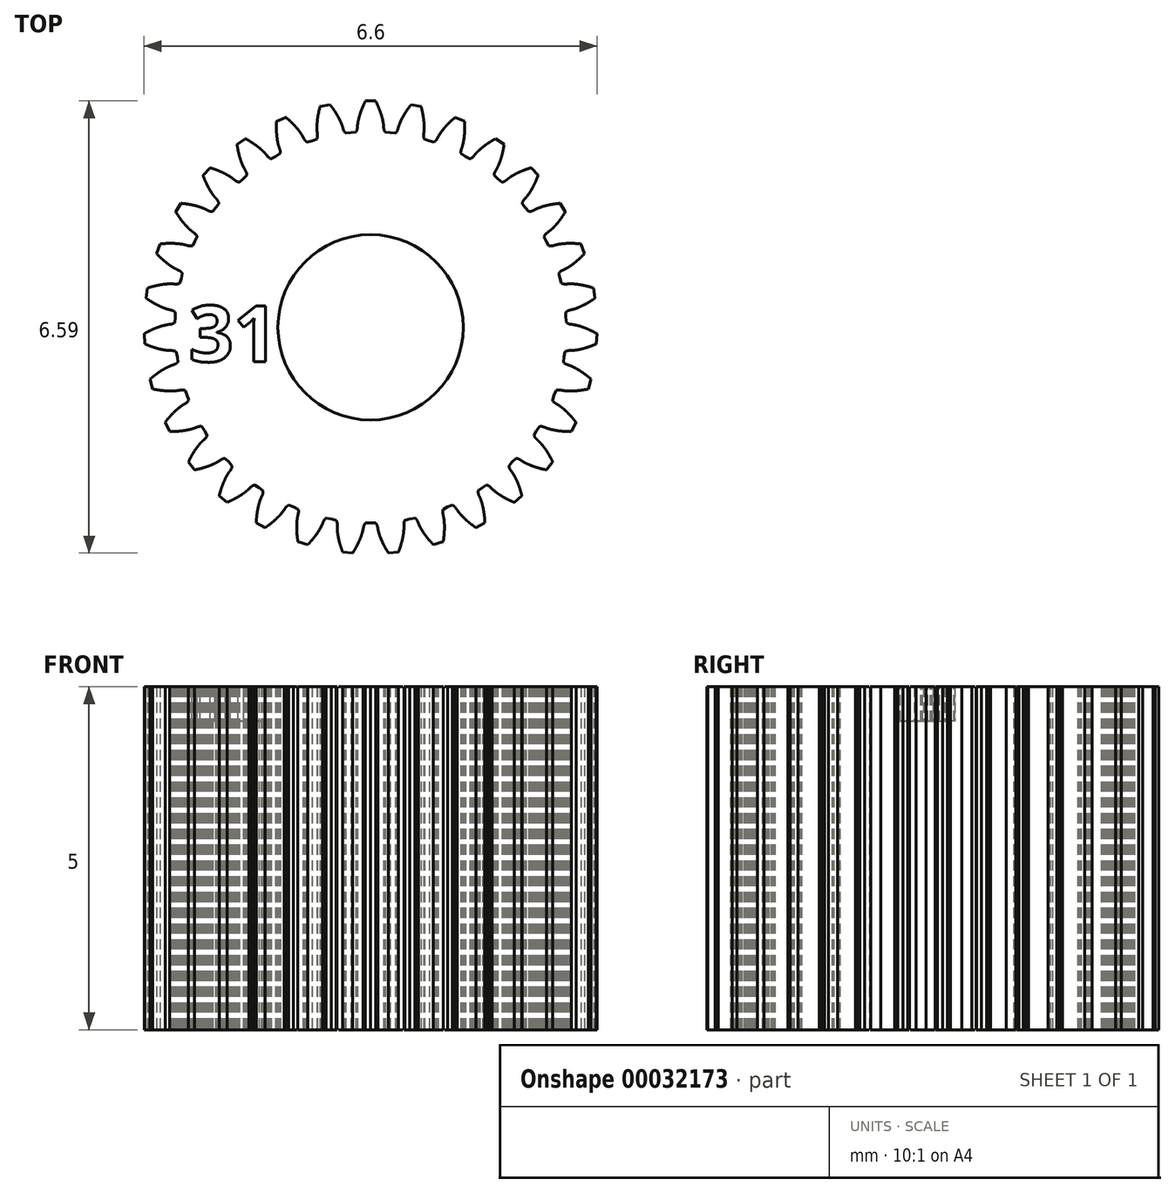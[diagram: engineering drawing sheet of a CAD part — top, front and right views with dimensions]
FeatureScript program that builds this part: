
annotation { "Feature Type Name" : "Feature", "Feature Type Description" : "" }
export const myFeature = defineFeature(function(context is Context, id is Id, definition is map)
    precondition{}
    {
        {
            var Q0;
            Q0=qCreatedBy(makeId("Top.planeOp"),FACE);
            var sketch = newSketch(context, id + "F0", { "sketchPlane" : qUnion([Q0])});
            skCircle(sketch, "E0", {"center": v(0, 0) * mm, "radius": 32.06 * mm});
            skCircle(sketch, "E1", {"center": v(0, 0) * mm, "radius": 0.2 * mm});
            skCircle(sketch, "E2", {"center": v(0, 0) * mm, "radius": 10.35 * mm});
            skCircle(sketch, "E3", {"center": v(0, 6.3) * mm, "radius": 0.2 * mm});
            skCircle(sketch, "E4", {"center": v(5.46, -3.15) * mm, "radius": 0.2 * mm});
            skCircle(sketch, "E5", {"center": v(-5.46, -3.15) * mm, "radius": 0.2 * mm});
            skLineSegment(sketch, "E6", {"start": v(0.26, 9.75) * mm, "end": v(0.26, 9.74) * mm});
            skLineSegment(sketch, "E7", {"start": v(0.26, 9.74) * mm, "end": v(0.26, 9.74) * mm});
            skLineSegment(sketch, "E8", {"start": v(0.26, 9.74) * mm, "end": v(0.26, 9.73) * mm});
            skLineSegment(sketch, "E9", {"start": v(0.26, 9.73) * mm, "end": v(0.25, 9.73) * mm});
            skLineSegment(sketch, "E10", {"start": v(0.25, 9.73) * mm, "end": v(0.25, 9.72) * mm});
            skLineSegment(sketch, "E11", {"start": v(0.25, 9.72) * mm, "end": v(0.25, 9.72) * mm});
            skLineSegment(sketch, "E12", {"start": v(0.25, 9.72) * mm, "end": v(0.25, 9.71) * mm});
            skLineSegment(sketch, "E13", {"start": v(0.25, 9.71) * mm, "end": v(0.24, 9.7) * mm});
            skLineSegment(sketch, "E14", {"start": v(0.24, 9.7) * mm, "end": v(0.24, 9.7) * mm});
            skLineSegment(sketch, "E15", {"start": v(0.24, 9.7) * mm, "end": v(0.24, 9.69) * mm});
            skLineSegment(sketch, "E16", {"start": v(0.24, 9.69) * mm, "end": v(0.23, 9.68) * mm});
            skLineSegment(sketch, "E17", {"start": v(0.23, 9.68) * mm, "end": v(0.23, 9.68) * mm});
            skLineSegment(sketch, "E18", {"start": v(0.23, 9.68) * mm, "end": v(0.23, 9.67) * mm});
            skLineSegment(sketch, "E19", {"start": v(0.23, 9.67) * mm, "end": v(0.23, 9.67) * mm});
            skLineSegment(sketch, "E20", {"start": v(0.23, 9.67) * mm, "end": v(0.22, 9.66) * mm});
            skLineSegment(sketch, "E21", {"start": v(0.22, 9.66) * mm, "end": v(0.22, 9.66) * mm});
            skLineSegment(sketch, "E22", {"start": v(0.22, 9.66) * mm, "end": v(0.22, 9.65) * mm});
            skLineSegment(sketch, "E23", {"start": v(0.22, 9.65) * mm, "end": v(0.22, 9.65) * mm});
            skLineSegment(sketch, "E24", {"start": v(0.22, 9.65) * mm, "end": v(0.22, 9.64) * mm});
            skLineSegment(sketch, "E25", {"start": v(0.22, 9.64) * mm, "end": v(0.21, 9.64) * mm});
            skLineSegment(sketch, "E26", {"start": v(0.21, 9.64) * mm, "end": v(0.21, 9.64) * mm});
            skLineSegment(sketch, "E27", {"start": v(0.21, 9.64) * mm, "end": v(0.21, 9.63) * mm});
            skLineSegment(sketch, "E28", {"start": v(0.21, 9.63) * mm, "end": v(0.2, 9.63) * mm});
            skLineSegment(sketch, "E29", {"start": v(0.2, 9.63) * mm, "end": v(0.2, 9.62) * mm});
            skLineSegment(sketch, "E30", {"start": v(0.2, 9.62) * mm, "end": v(0.2, 9.62) * mm});
            skLineSegment(sketch, "E31", {"start": v(0.2, 9.62) * mm, "end": v(0.2, 9.61) * mm});
            skLineSegment(sketch, "E32", {"start": v(0.2, 9.61) * mm, "end": v(0.2, 9.6) * mm});
            skLineSegment(sketch, "E33", {"start": v(0.2, 9.6) * mm, "end": v(0.2, 9.6) * mm});
            skLineSegment(sketch, "E34", {"start": v(0.2, 9.6) * mm, "end": v(0.2, 9.59) * mm});
            skLineSegment(sketch, "E35", {"start": v(0.2, 9.59) * mm, "end": v(0.2, 9.58) * mm});
            skLineSegment(sketch, "E36", {"start": v(0.2, 9.58) * mm, "end": v(0.19, 9.58) * mm});
            skLineSegment(sketch, "E37", {"start": v(0.19, 9.58) * mm, "end": v(0.19, 9.57) * mm});
            skLineSegment(sketch, "E38", {"start": v(0.19, 9.57) * mm, "end": v(0.18, 9.57) * mm});
            skLineSegment(sketch, "E39", {"start": v(0.18, 9.57) * mm, "end": v(0.18, 9.56) * mm});
            skLineSegment(sketch, "E40", {"start": v(0.18, 9.56) * mm, "end": v(0.18, 9.56) * mm});
            skLineSegment(sketch, "E41", {"start": v(0.18, 9.56) * mm, "end": v(0.18, 9.55) * mm});
            skLineSegment(sketch, "E42", {"start": v(0.18, 9.55) * mm, "end": v(0.18, 9.55) * mm});
            skLineSegment(sketch, "E43", {"start": v(0.18, 9.55) * mm, "end": v(0.17, 9.54) * mm});
            skLineSegment(sketch, "E44", {"start": v(0.17, 9.54) * mm, "end": v(0.17, 9.54) * mm});
            skLineSegment(sketch, "E45", {"start": v(0.17, 9.54) * mm, "end": v(0.17, 9.53) * mm});
            skLineSegment(sketch, "E46", {"start": v(0.17, 9.53) * mm, "end": v(0.17, 9.53) * mm});
            skLineSegment(sketch, "E47", {"start": v(0.17, 9.53) * mm, "end": v(0.17, 9.52) * mm});
            skLineSegment(sketch, "E48", {"start": v(0.17, 9.52) * mm, "end": v(0.16, 9.52) * mm});
            skLineSegment(sketch, "E49", {"start": v(0.16, 9.52) * mm, "end": v(0.16, 9.51) * mm});
            skLineSegment(sketch, "E50", {"start": v(0.16, 9.51) * mm, "end": v(0.16, 9.51) * mm});
            skLineSegment(sketch, "E51", {"start": v(0.16, 9.51) * mm, "end": v(0.16, 9.5) * mm});
            skLineSegment(sketch, "E52", {"start": v(0.16, 9.5) * mm, "end": v(0.16, 9.5) * mm});
            skLineSegment(sketch, "E53", {"start": v(0.16, 9.5) * mm, "end": v(0.15, 9.5) * mm});
            skLineSegment(sketch, "E54", {"start": v(0.15, 9.5) * mm, "end": v(0.15, 9.49) * mm});
            skLineSegment(sketch, "E55", {"start": v(0.15, 9.49) * mm, "end": v(0.15, 9.48) * mm});
            skLineSegment(sketch, "E56", {"start": v(0.15, 9.48) * mm, "end": v(0.15, 9.48) * mm});
            skLineSegment(sketch, "E57", {"start": v(0.15, 9.48) * mm, "end": v(0.15, 9.47) * mm});
            skLineSegment(sketch, "E58", {"start": v(0.15, 9.47) * mm, "end": v(0.15, 9.47) * mm});
            skLineSegment(sketch, "E59", {"start": v(0.15, 9.47) * mm, "end": v(0.14, 9.47) * mm});
            skLineSegment(sketch, "E60", {"start": v(0.14, 9.47) * mm, "end": v(0.14, 9.46) * mm});
            skLineSegment(sketch, "E61", {"start": v(0.14, 9.46) * mm, "end": v(0.14, 9.46) * mm});
            skLineSegment(sketch, "E62", {"start": v(0.14, 9.46) * mm, "end": v(0.14, 9.45) * mm});
            skLineSegment(sketch, "E63", {"start": v(0.14, 9.45) * mm, "end": v(0.14, 9.45) * mm});
            skLineSegment(sketch, "E64", {"start": v(0.14, 9.45) * mm, "end": v(0.14, 9.44) * mm});
            skLineSegment(sketch, "E65", {"start": v(0.14, 9.44) * mm, "end": v(0.13, 9.44) * mm});
            skLineSegment(sketch, "E66", {"start": v(0.13, 9.44) * mm, "end": v(0.13, 9.43) * mm});
            skLineSegment(sketch, "E67", {"start": v(0.13, 9.43) * mm, "end": v(0.13, 9.43) * mm});
            skLineSegment(sketch, "E68", {"start": v(0.13, 9.43) * mm, "end": v(0.13, 9.42) * mm});
            skLineSegment(sketch, "E69", {"start": v(0.13, 9.42) * mm, "end": v(0.13, 9.42) * mm});
            skLineSegment(sketch, "E70", {"start": v(0.13, 9.42) * mm, "end": v(0.12, 9.41) * mm});
            skLineSegment(sketch, "E71", {"start": v(0.12, 9.41) * mm, "end": v(0.12, 9.4) * mm});
            skLineSegment(sketch, "E72", {"start": v(0.12, 9.4) * mm, "end": v(0.12, 9.4) * mm});
            skLineSegment(sketch, "E73", {"start": v(0.12, 9.4) * mm, "end": v(0.12, 9.39) * mm});
            skLineSegment(sketch, "E74", {"start": v(0.12, 9.39) * mm, "end": v(0.12, 9.38) * mm});
            skLineSegment(sketch, "E75", {"start": v(0.12, 9.38) * mm, "end": v(0.11, 9.38) * mm});
            skLineSegment(sketch, "E76", {"start": v(0.11, 9.38) * mm, "end": v(0.11, 9.38) * mm});
            skLineSegment(sketch, "E77", {"start": v(0.11, 9.38) * mm, "end": v(0.11, 9.37) * mm});
            skLineSegment(sketch, "E78", {"start": v(0.11, 9.37) * mm, "end": v(0.1, 9.37) * mm});
            skLineSegment(sketch, "E79", {"start": v(0.1, 9.37) * mm, "end": v(0.1, 9.36) * mm});
            skLineSegment(sketch, "E80", {"start": v(0.1, 9.36) * mm, "end": v(0.1, 9.36) * mm});
            skLineSegment(sketch, "E81", {"start": v(0.1, 9.36) * mm, "end": v(0.1, 9.35) * mm});
            skLineSegment(sketch, "E82", {"start": v(0.1, 9.35) * mm, "end": v(0.1, 9.35) * mm});
            skLineSegment(sketch, "E83", {"start": v(0.1, 9.35) * mm, "end": v(0.1, 9.34) * mm});
            skLineSegment(sketch, "E84", {"start": v(0.1, 9.34) * mm, "end": v(0.1, 9.34) * mm});
            skLineSegment(sketch, "E85", {"start": v(0.1, 9.34) * mm, "end": v(0.1, 9.33) * mm});
            skLineSegment(sketch, "E86", {"start": v(0.1, 9.33) * mm, "end": v(0.1, 9.33) * mm});
            skLineSegment(sketch, "E87", {"start": v(0.1, 9.33) * mm, "end": v(0.1, 9.32) * mm});
            skLineSegment(sketch, "E88", {"start": v(0.1, 9.32) * mm, "end": v(0.1, 9.32) * mm});
            skLineSegment(sketch, "E89", {"start": v(0.1, 9.32) * mm, "end": v(0.09, 9.31) * mm});
            skLineSegment(sketch, "E90", {"start": v(0.09, 9.31) * mm, "end": v(0.09, 9.3) * mm});
            skLineSegment(sketch, "E91", {"start": v(0.09, 9.3) * mm, "end": v(0.09, 9.3) * mm});
            skLineSegment(sketch, "E92", {"start": v(0.09, 9.3) * mm, "end": v(0, 9.3) * mm});
            skLineSegment(sketch, "E93", {"start": v(0, 9.3) * mm, "end": v(-0.09, 9.3) * mm});
            skLineSegment(sketch, "E94", {"start": v(-0.09, 9.3) * mm, "end": v(-0.09, 9.3) * mm});
            skLineSegment(sketch, "E95", {"start": v(-0.09, 9.3) * mm, "end": v(-0.09, 9.31) * mm});
            skLineSegment(sketch, "E96", {"start": v(-0.09, 9.31) * mm, "end": v(-0.1, 9.32) * mm});
            skLineSegment(sketch, "E97", {"start": v(-0.1, 9.32) * mm, "end": v(-0.1, 9.32) * mm});
            skLineSegment(sketch, "E98", {"start": v(-0.1, 9.32) * mm, "end": v(-0.1, 9.33) * mm});
            skLineSegment(sketch, "E99", {"start": v(-0.1, 9.33) * mm, "end": v(-0.1, 9.33) * mm});
            skLineSegment(sketch, "E100", {"start": v(-0.1, 9.33) * mm, "end": v(-0.1, 9.34) * mm});
            skLineSegment(sketch, "E101", {"start": v(-0.1, 9.34) * mm, "end": v(-0.1, 9.34) * mm});
            skLineSegment(sketch, "E102", {"start": v(-0.1, 9.34) * mm, "end": v(-0.1, 9.35) * mm});
            skLineSegment(sketch, "E103", {"start": v(-0.1, 9.35) * mm, "end": v(-0.1, 9.35) * mm});
            skLineSegment(sketch, "E104", {"start": v(-0.1, 9.35) * mm, "end": v(-0.1, 9.36) * mm});
            skLineSegment(sketch, "E105", {"start": v(-0.1, 9.36) * mm, "end": v(-0.1, 9.36) * mm});
            skLineSegment(sketch, "E106", {"start": v(-0.1, 9.36) * mm, "end": v(-0.1, 9.37) * mm});
            skLineSegment(sketch, "E107", {"start": v(-0.1, 9.37) * mm, "end": v(-0.11, 9.37) * mm});
            skLineSegment(sketch, "E108", {"start": v(-0.11, 9.37) * mm, "end": v(-0.11, 9.38) * mm});
            skLineSegment(sketch, "E109", {"start": v(-0.11, 9.38) * mm, "end": v(-0.11, 9.38) * mm});
            skLineSegment(sketch, "E110", {"start": v(-0.11, 9.38) * mm, "end": v(-0.12, 9.38) * mm});
            skLineSegment(sketch, "E111", {"start": v(-0.12, 9.38) * mm, "end": v(-0.12, 9.39) * mm});
            skLineSegment(sketch, "E112", {"start": v(-0.12, 9.39) * mm, "end": v(-0.12, 9.4) * mm});
            skLineSegment(sketch, "E113", {"start": v(-0.12, 9.4) * mm, "end": v(-0.12, 9.4) * mm});
            skLineSegment(sketch, "E114", {"start": v(-0.12, 9.4) * mm, "end": v(-0.12, 9.41) * mm});
            skLineSegment(sketch, "E115", {"start": v(-0.12, 9.41) * mm, "end": v(-0.13, 9.42) * mm});
            skLineSegment(sketch, "E116", {"start": v(-0.13, 9.42) * mm, "end": v(-0.13, 9.42) * mm});
            skLineSegment(sketch, "E117", {"start": v(-0.13, 9.42) * mm, "end": v(-0.13, 9.43) * mm});
            skLineSegment(sketch, "E118", {"start": v(-0.13, 9.43) * mm, "end": v(-0.13, 9.43) * mm});
            skLineSegment(sketch, "E119", {"start": v(-0.13, 9.43) * mm, "end": v(-0.13, 9.44) * mm});
            skLineSegment(sketch, "E120", {"start": v(-0.13, 9.44) * mm, "end": v(-0.14, 9.44) * mm});
            skLineSegment(sketch, "E121", {"start": v(-0.14, 9.44) * mm, "end": v(-0.14, 9.45) * mm});
            skLineSegment(sketch, "E122", {"start": v(-0.14, 9.45) * mm, "end": v(-0.14, 9.45) * mm});
            skLineSegment(sketch, "E123", {"start": v(-0.14, 9.45) * mm, "end": v(-0.14, 9.46) * mm});
            skLineSegment(sketch, "E124", {"start": v(-0.14, 9.46) * mm, "end": v(-0.14, 9.46) * mm});
            skLineSegment(sketch, "E125", {"start": v(-0.14, 9.46) * mm, "end": v(-0.14, 9.47) * mm});
            skLineSegment(sketch, "E126", {"start": v(-0.14, 9.47) * mm, "end": v(-0.15, 9.47) * mm});
            skLineSegment(sketch, "E127", {"start": v(-0.15, 9.47) * mm, "end": v(-0.15, 9.47) * mm});
            skLineSegment(sketch, "E128", {"start": v(-0.15, 9.47) * mm, "end": v(-0.15, 9.48) * mm});
            skLineSegment(sketch, "E129", {"start": v(-0.15, 9.48) * mm, "end": v(-0.15, 9.48) * mm});
            skLineSegment(sketch, "E130", {"start": v(-0.15, 9.48) * mm, "end": v(-0.15, 9.49) * mm});
            skLineSegment(sketch, "E131", {"start": v(-0.15, 9.49) * mm, "end": v(-0.15, 9.5) * mm});
            skLineSegment(sketch, "E132", {"start": v(-0.15, 9.5) * mm, "end": v(-0.16, 9.5) * mm});
            skLineSegment(sketch, "E133", {"start": v(-0.16, 9.5) * mm, "end": v(-0.16, 9.5) * mm});
            skLineSegment(sketch, "E134", {"start": v(-0.16, 9.5) * mm, "end": v(-0.16, 9.51) * mm});
            skLineSegment(sketch, "E135", {"start": v(-0.16, 9.51) * mm, "end": v(-0.16, 9.51) * mm});
            skLineSegment(sketch, "E136", {"start": v(-0.16, 9.51) * mm, "end": v(-0.16, 9.52) * mm});
            skLineSegment(sketch, "E137", {"start": v(-0.16, 9.52) * mm, "end": v(-0.17, 9.52) * mm});
            skLineSegment(sketch, "E138", {"start": v(-0.17, 9.52) * mm, "end": v(-0.17, 9.53) * mm});
            skLineSegment(sketch, "E139", {"start": v(-0.17, 9.53) * mm, "end": v(-0.17, 9.53) * mm});
            skLineSegment(sketch, "E140", {"start": v(-0.17, 9.53) * mm, "end": v(-0.17, 9.54) * mm});
            skLineSegment(sketch, "E141", {"start": v(-0.17, 9.54) * mm, "end": v(-0.17, 9.54) * mm});
            skLineSegment(sketch, "E142", {"start": v(-0.17, 9.54) * mm, "end": v(-0.18, 9.55) * mm});
            skLineSegment(sketch, "E143", {"start": v(-0.18, 9.55) * mm, "end": v(-0.18, 9.55) * mm});
            skLineSegment(sketch, "E144", {"start": v(-0.18, 9.55) * mm, "end": v(-0.18, 9.56) * mm});
            skLineSegment(sketch, "E145", {"start": v(-0.18, 9.56) * mm, "end": v(-0.18, 9.56) * mm});
            skLineSegment(sketch, "E146", {"start": v(-0.18, 9.56) * mm, "end": v(-0.18, 9.57) * mm});
            skLineSegment(sketch, "E147", {"start": v(-0.18, 9.57) * mm, "end": v(-0.19, 9.57) * mm});
            skLineSegment(sketch, "E148", {"start": v(-0.19, 9.57) * mm, "end": v(-0.19, 9.58) * mm});
            skLineSegment(sketch, "E149", {"start": v(-0.19, 9.58) * mm, "end": v(-0.2, 9.58) * mm});
            skLineSegment(sketch, "E150", {"start": v(-0.2, 9.58) * mm, "end": v(-0.2, 9.59) * mm});
            skLineSegment(sketch, "E151", {"start": v(-0.2, 9.59) * mm, "end": v(-0.2, 9.6) * mm});
            skLineSegment(sketch, "E152", {"start": v(-0.2, 9.6) * mm, "end": v(-0.2, 9.6) * mm});
            skLineSegment(sketch, "E153", {"start": v(-0.2, 9.6) * mm, "end": v(-0.2, 9.61) * mm});
            skLineSegment(sketch, "E154", {"start": v(-0.2, 9.61) * mm, "end": v(-0.2, 9.62) * mm});
            skLineSegment(sketch, "E155", {"start": v(-0.2, 9.62) * mm, "end": v(-0.2, 9.62) * mm});
            skLineSegment(sketch, "E156", {"start": v(-0.2, 9.62) * mm, "end": v(-0.2, 9.63) * mm});
            skLineSegment(sketch, "E157", {"start": v(-0.2, 9.63) * mm, "end": v(-0.21, 9.63) * mm});
            skLineSegment(sketch, "E158", {"start": v(-0.21, 9.63) * mm, "end": v(-0.21, 9.64) * mm});
            skLineSegment(sketch, "E159", {"start": v(-0.21, 9.64) * mm, "end": v(-0.21, 9.64) * mm});
            skLineSegment(sketch, "E160", {"start": v(-0.21, 9.64) * mm, "end": v(-0.22, 9.64) * mm});
            skLineSegment(sketch, "E161", {"start": v(-0.22, 9.64) * mm, "end": v(-0.22, 9.65) * mm});
            skLineSegment(sketch, "E162", {"start": v(-0.22, 9.65) * mm, "end": v(-0.22, 9.65) * mm});
            skLineSegment(sketch, "E163", {"start": v(-0.22, 9.65) * mm, "end": v(-0.22, 9.66) * mm});
            skLineSegment(sketch, "E164", {"start": v(-0.22, 9.66) * mm, "end": v(-0.22, 9.66) * mm});
            skLineSegment(sketch, "E165", {"start": v(-0.22, 9.66) * mm, "end": v(-0.23, 9.67) * mm});
            skLineSegment(sketch, "E166", {"start": v(-0.23, 9.67) * mm, "end": v(-0.23, 9.67) * mm});
            skLineSegment(sketch, "E167", {"start": v(-0.23, 9.67) * mm, "end": v(-0.23, 9.68) * mm});
            skLineSegment(sketch, "E168", {"start": v(-0.23, 9.68) * mm, "end": v(-0.23, 9.68) * mm});
            skLineSegment(sketch, "E169", {"start": v(-0.23, 9.68) * mm, "end": v(-0.24, 9.69) * mm});
            skLineSegment(sketch, "E170", {"start": v(-0.24, 9.69) * mm, "end": v(-0.24, 9.7) * mm});
            skLineSegment(sketch, "E171", {"start": v(-0.24, 9.7) * mm, "end": v(-0.24, 9.7) * mm});
            skLineSegment(sketch, "E172", {"start": v(-0.24, 9.7) * mm, "end": v(-0.25, 9.71) * mm});
            skLineSegment(sketch, "E173", {"start": v(-0.25, 9.71) * mm, "end": v(-0.25, 9.72) * mm});
            skLineSegment(sketch, "E174", {"start": v(-0.25, 9.72) * mm, "end": v(-0.25, 9.72) * mm});
            skLineSegment(sketch, "E175", {"start": v(-0.25, 9.72) * mm, "end": v(-0.25, 9.73) * mm});
            skLineSegment(sketch, "E176", {"start": v(-0.25, 9.73) * mm, "end": v(-0.26, 9.73) * mm});
            skLineSegment(sketch, "E177", {"start": v(-0.26, 9.73) * mm, "end": v(-0.26, 9.74) * mm});
            skLineSegment(sketch, "E178", {"start": v(-0.26, 9.74) * mm, "end": v(-0.26, 9.74) * mm});
            skLineSegment(sketch, "E179", {"start": v(-0.26, 9.74) * mm, "end": v(-0.26, 9.75) * mm});
            skLineSegment(sketch, "E180", {"start": v(-0.26, 9.75) * mm, "end": v(-0.38, 9.74) * mm});
            skLineSegment(sketch, "E181", {"start": v(-0.38, 9.74) * mm, "end": v(-0.38, 9.74) * mm});
            skLineSegment(sketch, "E182", {"start": v(-0.38, 9.74) * mm, "end": v(-0.39, 9.73) * mm});
            skLineSegment(sketch, "E183", {"start": v(-0.39, 9.73) * mm, "end": v(-0.39, 9.73) * mm});
            skLineSegment(sketch, "E184", {"start": v(-0.39, 9.73) * mm, "end": v(-0.39, 9.72) * mm});
            skLineSegment(sketch, "E185", {"start": v(-0.39, 9.72) * mm, "end": v(-0.4, 9.72) * mm});
            skLineSegment(sketch, "E186", {"start": v(-0.4, 9.72) * mm, "end": v(-0.4, 9.72) * mm});
            skLineSegment(sketch, "E187", {"start": v(-0.4, 9.72) * mm, "end": v(-0.4, 9.71) * mm});
            skLineSegment(sketch, "E188", {"start": v(-0.4, 9.71) * mm, "end": v(-0.4, 9.7) * mm});
            skLineSegment(sketch, "E189", {"start": v(-0.4, 9.7) * mm, "end": v(-0.4, 9.7) * mm});
            skLineSegment(sketch, "E190", {"start": v(-0.4, 9.7) * mm, "end": v(-0.4, 9.69) * mm});
            skLineSegment(sketch, "E191", {"start": v(-0.4, 9.69) * mm, "end": v(-0.4, 9.68) * mm});
            skLineSegment(sketch, "E192", {"start": v(-0.4, 9.68) * mm, "end": v(-0.4, 9.68) * mm});
            skLineSegment(sketch, "E193", {"start": v(-0.4, 9.68) * mm, "end": v(-0.4, 9.67) * mm});
            skLineSegment(sketch, "E194", {"start": v(-0.4, 9.67) * mm, "end": v(-0.4, 9.67) * mm});
            skLineSegment(sketch, "E195", {"start": v(-0.4, 9.67) * mm, "end": v(-0.41, 9.66) * mm});
            skLineSegment(sketch, "E196", {"start": v(-0.41, 9.66) * mm, "end": v(-0.41, 9.66) * mm});
            skLineSegment(sketch, "E197", {"start": v(-0.41, 9.66) * mm, "end": v(-0.42, 9.65) * mm});
            skLineSegment(sketch, "E198", {"start": v(-0.42, 9.65) * mm, "end": v(-0.42, 9.65) * mm});
            skLineSegment(sketch, "E199", {"start": v(-0.42, 9.65) * mm, "end": v(-0.42, 9.64) * mm});
            skLineSegment(sketch, "E200", {"start": v(-0.42, 9.64) * mm, "end": v(-0.42, 9.64) * mm});
            skLineSegment(sketch, "E201", {"start": v(-0.42, 9.64) * mm, "end": v(-0.42, 9.63) * mm});
            skLineSegment(sketch, "E202", {"start": v(-0.42, 9.63) * mm, "end": v(-0.42, 9.63) * mm});
            skLineSegment(sketch, "E203", {"start": v(-0.42, 9.63) * mm, "end": v(-0.43, 9.62) * mm});
            skLineSegment(sketch, "E204", {"start": v(-0.43, 9.62) * mm, "end": v(-0.43, 9.62) * mm});
            skLineSegment(sketch, "E205", {"start": v(-0.43, 9.62) * mm, "end": v(-0.43, 9.61) * mm});
            skLineSegment(sketch, "E206", {"start": v(-0.43, 9.61) * mm, "end": v(-0.43, 9.6) * mm});
            skLineSegment(sketch, "E207", {"start": v(-0.43, 9.6) * mm, "end": v(-0.43, 9.6) * mm});
            skLineSegment(sketch, "E208", {"start": v(-0.43, 9.6) * mm, "end": v(-0.44, 9.6) * mm});
            skLineSegment(sketch, "E209", {"start": v(-0.44, 9.6) * mm, "end": v(-0.44, 9.6) * mm});
            skLineSegment(sketch, "E210", {"start": v(-0.44, 9.6) * mm, "end": v(-0.44, 9.59) * mm});
            skLineSegment(sketch, "E211", {"start": v(-0.44, 9.59) * mm, "end": v(-0.44, 9.58) * mm});
            skLineSegment(sketch, "E212", {"start": v(-0.44, 9.58) * mm, "end": v(-0.44, 9.58) * mm});
            skLineSegment(sketch, "E213", {"start": v(-0.44, 9.58) * mm, "end": v(-0.44, 9.57) * mm});
            skLineSegment(sketch, "E214", {"start": v(2.8, -0.5) * mm, "end": v(2.82, -0.43) * mm});
            skLineSegment(sketch, "E215", {"start": v(2.82, -0.43) * mm, "end": v(2.83, -0.36) * mm});
            skLineSegment(sketch, "E216", {"start": v(2.83, -0.36) * mm, "end": v(2.84, -0.35) * mm});
            skLineSegment(sketch, "E217", {"start": v(2.84, -0.35) * mm, "end": v(2.84, -0.35) * mm});
            skLineSegment(sketch, "E218", {"start": v(2.84, -0.35) * mm, "end": v(2.85, -0.35) * mm});
            skLineSegment(sketch, "E219", {"start": v(2.85, -0.35) * mm, "end": v(2.85, -0.35) * mm});
            skLineSegment(sketch, "E220", {"start": v(2.85, -0.35) * mm, "end": v(2.86, -0.35) * mm});
            skLineSegment(sketch, "E221", {"start": v(2.86, -0.35) * mm, "end": v(2.86, -0.34) * mm});
            skLineSegment(sketch, "E222", {"start": v(2.86, -0.34) * mm, "end": v(2.87, -0.34) * mm});
            skLineSegment(sketch, "E223", {"start": v(2.87, -0.34) * mm, "end": v(2.87, -0.34) * mm});
            skLineSegment(sketch, "E224", {"start": v(2.87, -0.34) * mm, "end": v(2.88, -0.34) * mm});
            skLineSegment(sketch, "E225", {"start": v(2.88, -0.34) * mm, "end": v(2.88, -0.34) * mm});
            skLineSegment(sketch, "E226", {"start": v(2.88, -0.34) * mm, "end": v(2.89, -0.34) * mm});
            skLineSegment(sketch, "E227", {"start": v(2.89, -0.34) * mm, "end": v(2.9, -0.34) * mm});
            skLineSegment(sketch, "E228", {"start": v(2.9, -0.34) * mm, "end": v(2.9, -0.34) * mm});
            skLineSegment(sketch, "E229", {"start": v(2.9, -0.34) * mm, "end": v(2.91, -0.34) * mm});
            skLineSegment(sketch, "E230", {"start": v(2.91, -0.34) * mm, "end": v(2.92, -0.34) * mm});
            skLineSegment(sketch, "E231", {"start": v(2.92, -0.34) * mm, "end": v(2.92, -0.34) * mm});
            skLineSegment(sketch, "E232", {"start": v(2.92, -0.34) * mm, "end": v(2.93, -0.34) * mm});
            skLineSegment(sketch, "E233", {"start": v(2.93, -0.34) * mm, "end": v(2.93, -0.34) * mm});
            skLineSegment(sketch, "E234", {"start": v(2.93, -0.34) * mm, "end": v(2.94, -0.34) * mm});
            skLineSegment(sketch, "E235", {"start": v(2.94, -0.34) * mm, "end": v(2.94, -0.34) * mm});
            skLineSegment(sketch, "E236", {"start": v(2.94, -0.34) * mm, "end": v(2.95, -0.34) * mm});
            skLineSegment(sketch, "E237", {"start": v(2.95, -0.34) * mm, "end": v(2.95, -0.34) * mm});
            skLineSegment(sketch, "E238", {"start": v(2.95, -0.34) * mm, "end": v(2.96, -0.34) * mm});
            skLineSegment(sketch, "E239", {"start": v(2.96, -0.34) * mm, "end": v(2.96, -0.34) * mm});
            skLineSegment(sketch, "E240", {"start": v(2.96, -0.34) * mm, "end": v(2.97, -0.34) * mm});
            skLineSegment(sketch, "E241", {"start": v(2.97, -0.34) * mm, "end": v(2.97, -0.33) * mm});
            skLineSegment(sketch, "E242", {"start": v(2.97, -0.33) * mm, "end": v(2.98, -0.33) * mm});
            skLineSegment(sketch, "E243", {"start": v(2.98, -0.33) * mm, "end": v(2.98, -0.33) * mm});
            skLineSegment(sketch, "E244", {"start": v(2.98, -0.33) * mm, "end": v(2.99, -0.33) * mm});
            skLineSegment(sketch, "E245", {"start": v(2.99, -0.33) * mm, "end": v(3, -0.33) * mm});
            skLineSegment(sketch, "E246", {"start": v(3, -0.33) * mm, "end": v(3, -0.33) * mm});
            skLineSegment(sketch, "E247", {"start": v(3, -0.33) * mm, "end": v(3.01, -0.33) * mm});
            skLineSegment(sketch, "E248", {"start": v(3.01, -0.33) * mm, "end": v(3.02, -0.33) * mm});
            skLineSegment(sketch, "E249", {"start": v(3.02, -0.33) * mm, "end": v(3.02, -0.33) * mm});
            skLineSegment(sketch, "E250", {"start": v(3.02, -0.33) * mm, "end": v(3.03, -0.33) * mm});
            skLineSegment(sketch, "E251", {"start": v(3.03, -0.33) * mm, "end": v(3.03, -0.33) * mm});
            skLineSegment(sketch, "E252", {"start": v(3.03, -0.33) * mm, "end": v(3.04, -0.32) * mm});
            skLineSegment(sketch, "E253", {"start": v(3.04, -0.32) * mm, "end": v(3.04, -0.32) * mm});
            skLineSegment(sketch, "E254", {"start": v(3.04, -0.32) * mm, "end": v(3.05, -0.32) * mm});
            skLineSegment(sketch, "E255", {"start": v(3.05, -0.32) * mm, "end": v(3.05, -0.32) * mm});
            skLineSegment(sketch, "E256", {"start": v(3.05, -0.32) * mm, "end": v(3.06, -0.32) * mm});
            skLineSegment(sketch, "E257", {"start": v(3.06, -0.32) * mm, "end": v(3.06, -0.32) * mm});
            skLineSegment(sketch, "E258", {"start": v(3.06, -0.32) * mm, "end": v(3.07, -0.32) * mm});
            skLineSegment(sketch, "E259", {"start": v(3.07, -0.32) * mm, "end": v(3.07, -0.32) * mm});
            skLineSegment(sketch, "E260", {"start": v(3.07, -0.32) * mm, "end": v(3.08, -0.32) * mm});
            skLineSegment(sketch, "E261", {"start": v(3.08, -0.32) * mm, "end": v(3.08, -0.31) * mm});
            skLineSegment(sketch, "E262", {"start": v(3.08, -0.31) * mm, "end": v(3.09, -0.31) * mm});
            skLineSegment(sketch, "E263", {"start": v(3.09, -0.31) * mm, "end": v(3.1, -0.31) * mm});
            skLineSegment(sketch, "E264", {"start": v(3.1, -0.31) * mm, "end": v(3.1, -0.31) * mm});
            skLineSegment(sketch, "E265", {"start": v(3.1, -0.31) * mm, "end": v(3.1, -0.3) * mm});
            skLineSegment(sketch, "E266", {"start": v(3.1, -0.3) * mm, "end": v(3.1, -0.3) * mm});
            skLineSegment(sketch, "E267", {"start": v(3.1, -0.3) * mm, "end": v(3.11, -0.3) * mm});
            skLineSegment(sketch, "E268", {"start": v(3.11, -0.3) * mm, "end": v(3.12, -0.3) * mm});
            skLineSegment(sketch, "E269", {"start": v(3.12, -0.3) * mm, "end": v(3.12, -0.3) * mm});
            skLineSegment(sketch, "E270", {"start": v(3.12, -0.3) * mm, "end": v(3.13, -0.3) * mm});
            skLineSegment(sketch, "E271", {"start": v(3.13, -0.3) * mm, "end": v(3.13, -0.3) * mm});
            skLineSegment(sketch, "E272", {"start": v(3.13, -0.3) * mm, "end": v(3.14, -0.3) * mm});
            skLineSegment(sketch, "E273", {"start": v(3.14, -0.3) * mm, "end": v(3.14, -0.3) * mm});
            skLineSegment(sketch, "E274", {"start": v(3.14, -0.3) * mm, "end": v(3.15, -0.3) * mm});
            skLineSegment(sketch, "E275", {"start": v(3.15, -0.3) * mm, "end": v(3.15, -0.3) * mm});
            skLineSegment(sketch, "E276", {"start": v(3.15, -0.3) * mm, "end": v(3.16, -0.3) * mm});
            skLineSegment(sketch, "E277", {"start": v(3.16, -0.3) * mm, "end": v(3.16, -0.3) * mm});
            skLineSegment(sketch, "E278", {"start": v(3.16, -0.3) * mm, "end": v(3.17, -0.29) * mm});
            skLineSegment(sketch, "E279", {"start": v(3.17, -0.29) * mm, "end": v(3.17, -0.29) * mm});
            skLineSegment(sketch, "E280", {"start": v(3.17, -0.29) * mm, "end": v(3.18, -0.29) * mm});
            skLineSegment(sketch, "E281", {"start": v(3.18, -0.29) * mm, "end": v(3.18, -0.28) * mm});
            skLineSegment(sketch, "E282", {"start": v(3.18, -0.28) * mm, "end": v(3.19, -0.28) * mm});
            skLineSegment(sketch, "E283", {"start": v(3.19, -0.28) * mm, "end": v(3.2, -0.28) * mm});
            skLineSegment(sketch, "E284", {"start": v(3.2, -0.28) * mm, "end": v(3.2, -0.28) * mm});
            skLineSegment(sketch, "E285", {"start": v(3.2, -0.28) * mm, "end": v(3.21, -0.27) * mm});
            skLineSegment(sketch, "E286", {"start": v(3.21, -0.27) * mm, "end": v(3.22, -0.27) * mm});
            skLineSegment(sketch, "E287", {"start": v(3.22, -0.27) * mm, "end": v(3.22, -0.27) * mm});
            skLineSegment(sketch, "E288", {"start": v(3.22, -0.27) * mm, "end": v(3.23, -0.27) * mm});
            skLineSegment(sketch, "E289", {"start": v(3.23, -0.27) * mm, "end": v(3.23, -0.27) * mm});
            skLineSegment(sketch, "E290", {"start": v(3.23, -0.27) * mm, "end": v(3.24, -0.26) * mm});
            skLineSegment(sketch, "E291", {"start": v(3.24, -0.26) * mm, "end": v(3.24, -0.26) * mm});
            skLineSegment(sketch, "E292", {"start": v(3.24, -0.26) * mm, "end": v(3.25, -0.26) * mm});
            skLineSegment(sketch, "E293", {"start": v(3.25, -0.26) * mm, "end": v(3.25, -0.26) * mm});
            skLineSegment(sketch, "E294", {"start": v(3.25, -0.26) * mm, "end": v(3.26, -0.26) * mm});
            skLineSegment(sketch, "E295", {"start": v(3.26, -0.26) * mm, "end": v(3.26, -0.25) * mm});
            skLineSegment(sketch, "E296", {"start": v(3.26, -0.25) * mm, "end": v(3.27, -0.25) * mm});
            skLineSegment(sketch, "E297", {"start": v(3.27, -0.25) * mm, "end": v(3.27, -0.25) * mm});
            skLineSegment(sketch, "E298", {"start": v(3.27, -0.25) * mm, "end": v(3.28, -0.25) * mm});
            skLineSegment(sketch, "E299", {"start": v(3.28, -0.25) * mm, "end": v(3.28, -0.25) * mm});
            skLineSegment(sketch, "E300", {"start": v(3.28, -0.25) * mm, "end": v(3.29, -0.24) * mm});
            skLineSegment(sketch, "E301", {"start": v(3.29, -0.24) * mm, "end": v(3.3, -0.24) * mm});
            skLineSegment(sketch, "E302", {"start": v(3.3, -0.24) * mm, "end": v(3.3, -0.1) * mm});
            skLineSegment(sketch, "E303", {"start": v(3.3, -0.1) * mm, "end": v(3.3, -0.1) * mm});
            skLineSegment(sketch, "E304", {"start": v(3.3, -0.1) * mm, "end": v(3.29, -0.09) * mm});
            skLineSegment(sketch, "E305", {"start": v(3.29, -0.09) * mm, "end": v(3.29, -0.09) * mm});
            skLineSegment(sketch, "E306", {"start": v(3.29, -0.09) * mm, "end": v(3.28, -0.08) * mm});
            skLineSegment(sketch, "E307", {"start": v(3.28, -0.08) * mm, "end": v(3.28, -0.08) * mm});
            skLineSegment(sketch, "E308", {"start": v(3.28, -0.08) * mm, "end": v(3.27, -0.08) * mm});
            skLineSegment(sketch, "E309", {"start": v(3.27, -0.08) * mm, "end": v(3.27, -0.08) * mm});
            skLineSegment(sketch, "E310", {"start": v(3.27, -0.08) * mm, "end": v(3.26, -0.07) * mm});
            skLineSegment(sketch, "E311", {"start": v(3.26, -0.07) * mm, "end": v(3.26, -0.07) * mm});
            skLineSegment(sketch, "E312", {"start": v(3.26, -0.07) * mm, "end": v(3.25, -0.07) * mm});
            skLineSegment(sketch, "E313", {"start": v(3.25, -0.07) * mm, "end": v(3.25, -0.07) * mm});
            skLineSegment(sketch, "E314", {"start": v(3.25, -0.07) * mm, "end": v(3.25, -0.06) * mm});
            skLineSegment(sketch, "E315", {"start": v(3.25, -0.06) * mm, "end": v(3.24, -0.06) * mm});
            skLineSegment(sketch, "E316", {"start": v(3.24, -0.06) * mm, "end": v(3.24, -0.06) * mm});
            skLineSegment(sketch, "E317", {"start": v(3.24, -0.06) * mm, "end": v(3.23, -0.06) * mm});
            skLineSegment(sketch, "E318", {"start": v(3.23, -0.06) * mm, "end": v(3.23, -0.06) * mm});
            skLineSegment(sketch, "E319", {"start": v(3.23, -0.06) * mm, "end": v(3.22, -0.05) * mm});
            skLineSegment(sketch, "E320", {"start": v(3.22, -0.05) * mm, "end": v(3.22, -0.05) * mm});
            skLineSegment(sketch, "E321", {"start": v(3.22, -0.05) * mm, "end": v(3.21, -0.05) * mm});
            skLineSegment(sketch, "E322", {"start": v(3.21, -0.05) * mm, "end": v(3.2, -0.05) * mm});
            skLineSegment(sketch, "E323", {"start": v(3.2, -0.05) * mm, "end": v(3.2, -0.04) * mm});
            skLineSegment(sketch, "E324", {"start": v(3.2, -0.04) * mm, "end": v(3.2, -0.04) * mm});
            skLineSegment(sketch, "E325", {"start": v(3.2, -0.04) * mm, "end": v(3.19, -0.04) * mm});
            skLineSegment(sketch, "E326", {"start": v(3.19, -0.04) * mm, "end": v(3.18, -0.03) * mm});
            skLineSegment(sketch, "E327", {"start": v(3.18, -0.03) * mm, "end": v(3.18, -0.03) * mm});
            skLineSegment(sketch, "E328", {"start": v(3.18, -0.03) * mm, "end": v(3.17, -0.03) * mm});
            skLineSegment(sketch, "E329", {"start": v(3.17, -0.03) * mm, "end": v(3.17, -0.03) * mm});
            skLineSegment(sketch, "E330", {"start": v(3.17, -0.03) * mm, "end": v(3.16, -0.03) * mm});
            skLineSegment(sketch, "E331", {"start": v(3.16, -0.03) * mm, "end": v(3.16, -0.02) * mm});
            skLineSegment(sketch, "E332", {"start": v(3.16, -0.02) * mm, "end": v(3.16, -0.02) * mm});
            skLineSegment(sketch, "E333", {"start": v(3.16, -0.02) * mm, "end": v(3.15, -0.02) * mm});
            skLineSegment(sketch, "E334", {"start": v(3.15, -0.02) * mm, "end": v(3.15, -0.02) * mm});
            skLineSegment(sketch, "E335", {"start": v(3.15, -0.02) * mm, "end": v(3.14, -0.02) * mm});
            skLineSegment(sketch, "E336", {"start": v(3.14, -0.02) * mm, "end": v(3.14, -0.01) * mm});
            skLineSegment(sketch, "E337", {"start": v(3.14, -0.01) * mm, "end": v(3.13, -0.01) * mm});
            skLineSegment(sketch, "E338", {"start": v(3.13, -0.01) * mm, "end": v(3.13, -0.01) * mm});
            skLineSegment(sketch, "E339", {"start": v(3.13, -0.01) * mm, "end": v(3.12, 0) * mm});
            skLineSegment(sketch, "E340", {"start": v(3.12, 0) * mm, "end": v(3.12, 0) * mm});
            skLineSegment(sketch, "E341", {"start": v(3.12, 0) * mm, "end": v(3.11, 0) * mm});
            skLineSegment(sketch, "E342", {"start": v(3.11, 0) * mm, "end": v(3.1, 0) * mm});
            skLineSegment(sketch, "E343", {"start": v(3.1, 0) * mm, "end": v(3.1, 0) * mm});
            skLineSegment(sketch, "E344", {"start": v(3.1, 0) * mm, "end": v(3.09, 0) * mm});
            skLineSegment(sketch, "E345", {"start": v(3.09, 0) * mm, "end": v(3.08, 0) * mm});
            skLineSegment(sketch, "E346", {"start": v(3.08, 0) * mm, "end": v(3.08, 0) * mm});
            skLineSegment(sketch, "E347", {"start": v(3.08, 0) * mm, "end": v(3.07, 0) * mm});
            skLineSegment(sketch, "E348", {"start": v(3.07, 0) * mm, "end": v(3.07, 0.01) * mm});
            skLineSegment(sketch, "E349", {"start": v(3.07, 0.01) * mm, "end": v(3.07, 0.01) * mm});
            skLineSegment(sketch, "E350", {"start": v(3.07, 0.01) * mm, "end": v(3.06, 0.01) * mm});
            skLineSegment(sketch, "E351", {"start": v(3.06, 0.01) * mm, "end": v(3.06, 0.01) * mm});
            skLineSegment(sketch, "E352", {"start": v(3.06, 0.01) * mm, "end": v(3.05, 0.02) * mm});
            skLineSegment(sketch, "E353", {"start": v(3.05, 0.02) * mm, "end": v(3.05, 0.02) * mm});
            skLineSegment(sketch, "E354", {"start": v(3.05, 0.02) * mm, "end": v(3.04, 0.02) * mm});
            skLineSegment(sketch, "E355", {"start": v(3.04, 0.02) * mm, "end": v(3.04, 0.02) * mm});
            skLineSegment(sketch, "E356", {"start": v(3.04, 0.02) * mm, "end": v(3.03, 0.02) * mm});
            skLineSegment(sketch, "E357", {"start": v(3.03, 0.02) * mm, "end": v(3.03, 0.02) * mm});
            skLineSegment(sketch, "E358", {"start": v(3.03, 0.02) * mm, "end": v(3.02, 0.03) * mm});
            skLineSegment(sketch, "E359", {"start": v(3.02, 0.03) * mm, "end": v(3.02, 0.03) * mm});
            skLineSegment(sketch, "E360", {"start": v(3.02, 0.03) * mm, "end": v(3.01, 0.03) * mm});
            skLineSegment(sketch, "E361", {"start": v(3.01, 0.03) * mm, "end": v(3, 0.03) * mm});
            skLineSegment(sketch, "E362", {"start": v(3, 0.03) * mm, "end": v(3, 0.03) * mm});
            skLineSegment(sketch, "E363", {"start": v(3, 0.03) * mm, "end": v(2.99, 0.03) * mm});
            skLineSegment(sketch, "E364", {"start": v(2.99, 0.03) * mm, "end": v(2.98, 0.03) * mm});
            skLineSegment(sketch, "E365", {"start": v(2.98, 0.03) * mm, "end": v(2.98, 0.03) * mm});
            skLineSegment(sketch, "E366", {"start": v(2.98, 0.03) * mm, "end": v(2.98, 0.04) * mm});
            skLineSegment(sketch, "E367", {"start": v(2.98, 0.04) * mm, "end": v(2.97, 0.04) * mm});
            skLineSegment(sketch, "E368", {"start": v(2.97, 0.04) * mm, "end": v(2.97, 0.04) * mm});
            skLineSegment(sketch, "E369", {"start": v(2.97, 0.04) * mm, "end": v(2.96, 0.04) * mm});
            skLineSegment(sketch, "E370", {"start": v(2.96, 0.04) * mm, "end": v(2.96, 0.04) * mm});
            skLineSegment(sketch, "E371", {"start": v(2.96, 0.04) * mm, "end": v(2.95, 0.04) * mm});
            skLineSegment(sketch, "E372", {"start": v(2.95, 0.04) * mm, "end": v(2.95, 0.04) * mm});
            skLineSegment(sketch, "E373", {"start": v(2.95, 0.04) * mm, "end": v(2.94, 0.04) * mm});
            skLineSegment(sketch, "E374", {"start": v(2.94, 0.04) * mm, "end": v(2.94, 0.04) * mm});
            skLineSegment(sketch, "E375", {"start": v(2.94, 0.04) * mm, "end": v(2.93, 0.04) * mm});
            skLineSegment(sketch, "E376", {"start": v(2.93, 0.04) * mm, "end": v(2.93, 0.04) * mm});
            skLineSegment(sketch, "E377", {"start": v(2.93, 0.04) * mm, "end": v(2.92, 0.04) * mm});
            skLineSegment(sketch, "E378", {"start": v(2.92, 0.04) * mm, "end": v(2.92, 0.04) * mm});
            skLineSegment(sketch, "E379", {"start": v(2.92, 0.04) * mm, "end": v(2.91, 0.04) * mm});
            skLineSegment(sketch, "E380", {"start": v(2.91, 0.04) * mm, "end": v(2.9, 0.05) * mm});
            skLineSegment(sketch, "E381", {"start": v(2.9, 0.05) * mm, "end": v(2.9, 0.05) * mm});
            skLineSegment(sketch, "E382", {"start": v(2.9, 0.05) * mm, "end": v(2.89, 0.05) * mm});
            skLineSegment(sketch, "E383", {"start": v(2.89, 0.05) * mm, "end": v(2.88, 0.05) * mm});
            skLineSegment(sketch, "E384", {"start": v(2.88, 0.05) * mm, "end": v(2.88, 0.05) * mm});
            skLineSegment(sketch, "E385", {"start": v(2.88, 0.05) * mm, "end": v(2.87, 0.06) * mm});
            skLineSegment(sketch, "E386", {"start": v(2.87, 0.06) * mm, "end": v(2.87, 0.06) * mm});
            skLineSegment(sketch, "E387", {"start": v(2.87, 0.06) * mm, "end": v(2.86, 0.06) * mm});
            skLineSegment(sketch, "E388", {"start": v(2.86, 0.06) * mm, "end": v(2.86, 0.07) * mm});
            skLineSegment(sketch, "E389", {"start": v(2.86, 0.07) * mm, "end": v(2.85, 0.07) * mm});
            skLineSegment(sketch, "E390", {"start": v(2.95, 6.23) * mm, "end": v(2.95, 6.3) * mm});
            skLineSegment(sketch, "E391", {"start": v(2.95, 6.3) * mm, "end": v(2.95, 6.37) * mm});
            skLineSegment(sketch, "E392", {"start": v(2.95, 6.37) * mm, "end": v(2.96, 6.38) * mm});
            skLineSegment(sketch, "E393", {"start": v(2.96, 6.38) * mm, "end": v(2.96, 6.38) * mm});
            skLineSegment(sketch, "E394", {"start": v(2.96, 6.38) * mm, "end": v(2.97, 6.39) * mm});
            skLineSegment(sketch, "E395", {"start": v(2.97, 6.39) * mm, "end": v(2.97, 6.39) * mm});
            skLineSegment(sketch, "E396", {"start": v(2.97, 6.39) * mm, "end": v(2.98, 6.4) * mm});
            skLineSegment(sketch, "E397", {"start": v(2.98, 6.4) * mm, "end": v(2.98, 6.4) * mm});
            skLineSegment(sketch, "E398", {"start": v(2.98, 6.4) * mm, "end": v(2.99, 6.4) * mm});
            skLineSegment(sketch, "E399", {"start": v(2.99, 6.4) * mm, "end": v(3, 6.4) * mm});
            skLineSegment(sketch, "E400", {"start": v(3, 6.4) * mm, "end": v(3, 6.4) * mm});
            skLineSegment(sketch, "E401", {"start": v(3, 6.4) * mm, "end": v(3.01, 6.4) * mm});
            skLineSegment(sketch, "E402", {"start": v(3.01, 6.4) * mm, "end": v(3.02, 6.4) * mm});
            skLineSegment(sketch, "E403", {"start": v(3.02, 6.4) * mm, "end": v(3.02, 6.4) * mm});
            skLineSegment(sketch, "E404", {"start": v(3.02, 6.4) * mm, "end": v(3.03, 6.4) * mm});
            skLineSegment(sketch, "E405", {"start": v(3.03, 6.4) * mm, "end": v(3.03, 6.4) * mm});
            skLineSegment(sketch, "E406", {"start": v(3.03, 6.4) * mm, "end": v(3.04, 6.4) * mm});
            skLineSegment(sketch, "E407", {"start": v(3.04, 6.4) * mm, "end": v(3.04, 6.4) * mm});
            skLineSegment(sketch, "E408", {"start": v(3.04, 6.4) * mm, "end": v(3.05, 6.4) * mm});
            skLineSegment(sketch, "E409", {"start": v(3.05, 6.4) * mm, "end": v(3.05, 6.4) * mm});
            skLineSegment(sketch, "E410", {"start": v(3.05, 6.4) * mm, "end": v(3.06, 6.41) * mm});
            skLineSegment(sketch, "E411", {"start": v(3.06, 6.41) * mm, "end": v(3.06, 6.41) * mm});
            skLineSegment(sketch, "E412", {"start": v(3.06, 6.41) * mm, "end": v(3.07, 6.41) * mm});
            skLineSegment(sketch, "E413", {"start": v(3.07, 6.41) * mm, "end": v(3.07, 6.42) * mm});
            skLineSegment(sketch, "E414", {"start": v(3.07, 6.42) * mm, "end": v(3.08, 6.42) * mm});
            skLineSegment(sketch, "E415", {"start": v(3.08, 6.42) * mm, "end": v(3.08, 6.42) * mm});
            skLineSegment(sketch, "E416", {"start": v(3.08, 6.42) * mm, "end": v(3.09, 6.42) * mm});
            skLineSegment(sketch, "E417", {"start": v(3.09, 6.42) * mm, "end": v(3.1, 6.42) * mm});
            skLineSegment(sketch, "E418", {"start": v(3.1, 6.42) * mm, "end": v(3.1, 6.42) * mm});
            skLineSegment(sketch, "E419", {"start": v(3.1, 6.42) * mm, "end": v(3.1, 6.43) * mm});
            skLineSegment(sketch, "E420", {"start": v(3.1, 6.43) * mm, "end": v(3.11, 6.43) * mm});
            skLineSegment(sketch, "E421", {"start": v(3.11, 6.43) * mm, "end": v(3.12, 6.43) * mm});
            skLineSegment(sketch, "E422", {"start": v(3.12, 6.43) * mm, "end": v(3.12, 6.43) * mm});
            skLineSegment(sketch, "E423", {"start": v(3.12, 6.43) * mm, "end": v(3.13, 6.43) * mm});
            skLineSegment(sketch, "E424", {"start": v(3.13, 6.43) * mm, "end": v(3.13, 6.43) * mm});
            skLineSegment(sketch, "E425", {"start": v(3.13, 6.43) * mm, "end": v(3.14, 6.43) * mm});
            skLineSegment(sketch, "E426", {"start": v(3.14, 6.43) * mm, "end": v(3.14, 6.44) * mm});
            skLineSegment(sketch, "E427", {"start": v(3.14, 6.44) * mm, "end": v(3.15, 6.44) * mm});
            skLineSegment(sketch, "E428", {"start": v(3.15, 6.44) * mm, "end": v(3.15, 6.44) * mm});
            skLineSegment(sketch, "E429", {"start": v(3.15, 6.44) * mm, "end": v(3.16, 6.44) * mm});
            skLineSegment(sketch, "E430", {"start": v(3.16, 6.44) * mm, "end": v(3.16, 6.44) * mm});
            skLineSegment(sketch, "E431", {"start": v(3.16, 6.44) * mm, "end": v(3.17, 6.45) * mm});
            skLineSegment(sketch, "E432", {"start": v(3.17, 6.45) * mm, "end": v(3.17, 6.45) * mm});
            skLineSegment(sketch, "E433", {"start": v(3.17, 6.45) * mm, "end": v(3.18, 6.45) * mm});
            skLineSegment(sketch, "E434", {"start": v(3.18, 6.45) * mm, "end": v(3.18, 6.45) * mm});
            skLineSegment(sketch, "E435", {"start": v(3.18, 6.45) * mm, "end": v(3.19, 6.45) * mm});
            skLineSegment(sketch, "E436", {"start": v(3.19, 6.45) * mm, "end": v(3.2, 6.46) * mm});
            skLineSegment(sketch, "E437", {"start": v(3.2, 6.46) * mm, "end": v(3.2, 6.46) * mm});
            skLineSegment(sketch, "E438", {"start": v(3.2, 6.46) * mm, "end": v(3.21, 6.46) * mm});
            skLineSegment(sketch, "E439", {"start": v(3.21, 6.46) * mm, "end": v(3.22, 6.47) * mm});
            skLineSegment(sketch, "E440", {"start": v(3.22, 6.47) * mm, "end": v(3.22, 6.47) * mm});
            skLineSegment(sketch, "E441", {"start": v(3.22, 6.47) * mm, "end": v(3.23, 6.47) * mm});
            skLineSegment(sketch, "E442", {"start": v(3.23, 6.47) * mm, "end": v(3.23, 6.47) * mm});
            skLineSegment(sketch, "E443", {"start": v(3.23, 6.47) * mm, "end": v(3.24, 6.48) * mm});
            skLineSegment(sketch, "E444", {"start": v(3.24, 6.48) * mm, "end": v(3.24, 6.48) * mm});
            skLineSegment(sketch, "E445", {"start": v(3.24, 6.48) * mm, "end": v(3.25, 6.48) * mm});
            skLineSegment(sketch, "E446", {"start": v(3.25, 6.48) * mm, "end": v(3.25, 6.48) * mm});
            skLineSegment(sketch, "E447", {"start": v(3.25, 6.48) * mm, "end": v(3.26, 6.48) * mm});
            skLineSegment(sketch, "E448", {"start": v(3.26, 6.48) * mm, "end": v(3.26, 6.49) * mm});
            skLineSegment(sketch, "E449", {"start": v(3.26, 6.49) * mm, "end": v(3.26, 6.49) * mm});
            skLineSegment(sketch, "E450", {"start": v(3.26, 6.49) * mm, "end": v(3.27, 6.5) * mm});
            skLineSegment(sketch, "E451", {"start": v(3.27, 6.5) * mm, "end": v(3.27, 6.5) * mm});
            skLineSegment(sketch, "E452", {"start": v(3.27, 6.5) * mm, "end": v(3.28, 6.5) * mm});
            skLineSegment(sketch, "E453", {"start": v(3.28, 6.5) * mm, "end": v(3.28, 6.5) * mm});
            skLineSegment(sketch, "E454", {"start": v(3.28, 6.5) * mm, "end": v(3.29, 6.5) * mm});
            skLineSegment(sketch, "E455", {"start": v(3.29, 6.5) * mm, "end": v(3.3, 6.5) * mm});
            skLineSegment(sketch, "E456", {"start": v(3.3, 6.5) * mm, "end": v(3.3, 6.5) * mm});
            skLineSegment(sketch, "E457", {"start": v(3.3, 6.5) * mm, "end": v(3.3, 6.51) * mm});
            skLineSegment(sketch, "E458", {"start": v(3.3, 6.51) * mm, "end": v(3.31, 6.51) * mm});
            skLineSegment(sketch, "E459", {"start": v(3.31, 6.51) * mm, "end": v(3.32, 6.52) * mm});
            skLineSegment(sketch, "E460", {"start": v(3.32, 6.52) * mm, "end": v(3.32, 6.52) * mm});
            skLineSegment(sketch, "E461", {"start": v(3.32, 6.52) * mm, "end": v(3.33, 6.52) * mm});
            skLineSegment(sketch, "E462", {"start": v(3.33, 6.52) * mm, "end": v(3.33, 6.52) * mm});
            skLineSegment(sketch, "E463", {"start": v(3.33, 6.52) * mm, "end": v(3.33, 6.53) * mm});
            skLineSegment(sketch, "E464", {"start": v(3.33, 6.53) * mm, "end": v(3.34, 6.53) * mm});
            skLineSegment(sketch, "E465", {"start": v(3.34, 6.53) * mm, "end": v(3.34, 6.53) * mm});
            skLineSegment(sketch, "E466", {"start": v(3.34, 6.53) * mm, "end": v(3.35, 6.53) * mm});
            skLineSegment(sketch, "E467", {"start": v(3.35, 6.53) * mm, "end": v(3.35, 6.54) * mm});
            skLineSegment(sketch, "E468", {"start": v(3.35, 6.54) * mm, "end": v(3.36, 6.54) * mm});
            skLineSegment(sketch, "E469", {"start": v(3.36, 6.54) * mm, "end": v(3.36, 6.54) * mm});
            skLineSegment(sketch, "E470", {"start": v(3.36, 6.54) * mm, "end": v(3.37, 6.55) * mm});
            skLineSegment(sketch, "E471", {"start": v(3.37, 6.55) * mm, "end": v(3.37, 6.55) * mm});
            skLineSegment(sketch, "E472", {"start": v(3.37, 6.55) * mm, "end": v(3.38, 6.55) * mm});
            skLineSegment(sketch, "E473", {"start": v(3.38, 6.55) * mm, "end": v(3.38, 6.55) * mm});
            skLineSegment(sketch, "E474", {"start": v(3.38, 6.55) * mm, "end": v(3.39, 6.56) * mm});
            skLineSegment(sketch, "E475", {"start": v(3.39, 6.56) * mm, "end": v(3.4, 6.56) * mm});
            skLineSegment(sketch, "E476", {"start": v(3.4, 6.56) * mm, "end": v(3.38, 6.7) * mm});
            skLineSegment(sketch, "E477", {"start": v(3.38, 6.7) * mm, "end": v(3.37, 6.7) * mm});
            skLineSegment(sketch, "E478", {"start": v(3.37, 6.7) * mm, "end": v(3.37, 6.71) * mm});
            skLineSegment(sketch, "E479", {"start": v(3.37, 6.71) * mm, "end": v(3.36, 6.71) * mm});
            skLineSegment(sketch, "E480", {"start": v(3.36, 6.71) * mm, "end": v(3.36, 6.71) * mm});
            skLineSegment(sketch, "E481", {"start": v(3.36, 6.71) * mm, "end": v(3.35, 6.72) * mm});
            skLineSegment(sketch, "E482", {"start": v(3.35, 6.72) * mm, "end": v(3.35, 6.72) * mm});
            skLineSegment(sketch, "E483", {"start": v(3.35, 6.72) * mm, "end": v(3.34, 6.72) * mm});
            skLineSegment(sketch, "E484", {"start": v(3.34, 6.72) * mm, "end": v(3.34, 6.72) * mm});
            skLineSegment(sketch, "E485", {"start": v(3.34, 6.72) * mm, "end": v(3.33, 6.72) * mm});
            skLineSegment(sketch, "E486", {"start": v(3.33, 6.72) * mm, "end": v(3.33, 6.72) * mm});
            skLineSegment(sketch, "E487", {"start": v(3.33, 6.72) * mm, "end": v(3.32, 6.73) * mm});
            skLineSegment(sketch, "E488", {"start": v(3.32, 6.73) * mm, "end": v(3.32, 6.73) * mm});
            skLineSegment(sketch, "E489", {"start": v(3.32, 6.73) * mm, "end": v(3.31, 6.73) * mm});
            skLineSegment(sketch, "E490", {"start": v(3.31, 6.73) * mm, "end": v(3.3, 6.73) * mm});
            skLineSegment(sketch, "E491", {"start": v(3.3, 6.73) * mm, "end": v(3.3, 6.73) * mm});
            skLineSegment(sketch, "E492", {"start": v(3.3, 6.73) * mm, "end": v(3.3, 6.74) * mm});
            skLineSegment(sketch, "E493", {"start": v(3.3, 6.74) * mm, "end": v(3.3, 6.74) * mm});
            skLineSegment(sketch, "E494", {"start": v(3.3, 6.74) * mm, "end": v(3.29, 6.74) * mm});
            skLineSegment(sketch, "E495", {"start": v(3.29, 6.74) * mm, "end": v(3.28, 6.74) * mm});
            skLineSegment(sketch, "E496", {"start": v(3.28, 6.74) * mm, "end": v(3.28, 6.74) * mm});
            skLineSegment(sketch, "E497", {"start": v(3.28, 6.74) * mm, "end": v(3.27, 6.74) * mm});
            skLineSegment(sketch, "E498", {"start": v(3.27, 6.74) * mm, "end": v(3.27, 6.74) * mm});
            skLineSegment(sketch, "E499", {"start": v(3.27, 6.74) * mm, "end": v(3.26, 6.75) * mm});
            skLineSegment(sketch, "E500", {"start": v(3.26, 6.75) * mm, "end": v(3.26, 6.75) * mm});
            skLineSegment(sketch, "E501", {"start": v(3.26, 6.75) * mm, "end": v(3.25, 6.75) * mm});
            skLineSegment(sketch, "E502", {"start": v(3.25, 6.75) * mm, "end": v(3.25, 6.75) * mm});
            skLineSegment(sketch, "E503", {"start": v(3.25, 6.75) * mm, "end": v(3.24, 6.75) * mm});
            skLineSegment(sketch, "E504", {"start": v(3.24, 6.75) * mm, "end": v(3.24, 6.75) * mm});
            skLineSegment(sketch, "E505", {"start": v(3.24, 6.75) * mm, "end": v(3.23, 6.75) * mm});
            skLineSegment(sketch, "E506", {"start": v(3.23, 6.75) * mm, "end": v(3.23, 6.75) * mm});
            skLineSegment(sketch, "E507", {"start": v(3.23, 6.75) * mm, "end": v(3.22, 6.76) * mm});
            skLineSegment(sketch, "E508", {"start": v(3.22, 6.76) * mm, "end": v(3.22, 6.76) * mm});
            skLineSegment(sketch, "E509", {"start": v(3.22, 6.76) * mm, "end": v(3.21, 6.76) * mm});
            skLineSegment(sketch, "E510", {"start": v(3.21, 6.76) * mm, "end": v(3.2, 6.76) * mm});
            skLineSegment(sketch, "E511", {"start": v(3.2, 6.76) * mm, "end": v(3.2, 6.76) * mm});
            skLineSegment(sketch, "E512", {"start": v(3.2, 6.76) * mm, "end": v(3.19, 6.77) * mm});
            skLineSegment(sketch, "E513", {"start": v(3.19, 6.77) * mm, "end": v(3.18, 6.77) * mm});
            skLineSegment(sketch, "E514", {"start": v(3.18, 6.77) * mm, "end": v(3.18, 6.77) * mm});
            skLineSegment(sketch, "E515", {"start": v(3.18, 6.77) * mm, "end": v(3.17, 6.77) * mm});
            skLineSegment(sketch, "E516", {"start": v(3.17, 6.77) * mm, "end": v(3.17, 6.77) * mm});
            skLineSegment(sketch, "E517", {"start": v(3.17, 6.77) * mm, "end": v(3.16, 6.77) * mm});
            skLineSegment(sketch, "E518", {"start": v(3.16, 6.77) * mm, "end": v(3.16, 6.77) * mm});
            skLineSegment(sketch, "E519", {"start": v(3.16, 6.77) * mm, "end": v(3.15, 6.77) * mm});
            skLineSegment(sketch, "E520", {"start": v(3.15, 6.77) * mm, "end": v(3.15, 6.77) * mm});
            skLineSegment(sketch, "E521", {"start": v(3.15, 6.77) * mm, "end": v(3.14, 6.77) * mm});
            skLineSegment(sketch, "E522", {"start": v(3.14, 6.77) * mm, "end": v(3.14, 6.77) * mm});
            skLineSegment(sketch, "E523", {"start": v(3.14, 6.77) * mm, "end": v(3.13, 6.78) * mm});
            skLineSegment(sketch, "E524", {"start": v(3.13, 6.78) * mm, "end": v(3.13, 6.78) * mm});
            skLineSegment(sketch, "E525", {"start": v(3.13, 6.78) * mm, "end": v(3.12, 6.78) * mm});
            skLineSegment(sketch, "E526", {"start": v(3.12, 6.78) * mm, "end": v(3.12, 6.78) * mm});
            skLineSegment(sketch, "E527", {"start": v(3.12, 6.78) * mm, "end": v(3.11, 6.78) * mm});
            skLineSegment(sketch, "E528", {"start": v(3.11, 6.78) * mm, "end": v(3.1, 6.78) * mm});
            skLineSegment(sketch, "E529", {"start": v(3.1, 6.78) * mm, "end": v(3.1, 6.78) * mm});
            skLineSegment(sketch, "E530", {"start": v(3.1, 6.78) * mm, "end": v(3.09, 6.78) * mm});
            skLineSegment(sketch, "E531", {"start": v(3.09, 6.78) * mm, "end": v(3.08, 6.78) * mm});
            skLineSegment(sketch, "E532", {"start": v(3.08, 6.78) * mm, "end": v(3.08, 6.78) * mm});
            skLineSegment(sketch, "E533", {"start": v(3.08, 6.78) * mm, "end": v(3.07, 6.78) * mm});
            skLineSegment(sketch, "E534", {"start": v(3.07, 6.78) * mm, "end": v(3.07, 6.78) * mm});
            skLineSegment(sketch, "E535", {"start": v(3.07, 6.78) * mm, "end": v(3.06, 6.78) * mm});
            skLineSegment(sketch, "E536", {"start": v(3.06, 6.78) * mm, "end": v(3.06, 6.79) * mm});
            skLineSegment(sketch, "E537", {"start": v(3.06, 6.79) * mm, "end": v(3.06, 6.79) * mm});
            skLineSegment(sketch, "E538", {"start": v(3.06, 6.79) * mm, "end": v(3.05, 6.79) * mm});
            skLineSegment(sketch, "E539", {"start": v(3.05, 6.79) * mm, "end": v(3.05, 6.79) * mm});
            skLineSegment(sketch, "E540", {"start": v(3.05, 6.79) * mm, "end": v(3.04, 6.79) * mm});
            skLineSegment(sketch, "E541", {"start": v(3.04, 6.79) * mm, "end": v(3.04, 6.79) * mm});
            skLineSegment(sketch, "E542", {"start": v(3.04, 6.79) * mm, "end": v(3.03, 6.79) * mm});
            skLineSegment(sketch, "E543", {"start": v(3.03, 6.79) * mm, "end": v(3.03, 6.79) * mm});
            skLineSegment(sketch, "E544", {"start": v(3.03, 6.79) * mm, "end": v(3.02, 6.79) * mm});
            skLineSegment(sketch, "E545", {"start": v(3.02, 6.79) * mm, "end": v(3.02, 6.79) * mm});
            skLineSegment(sketch, "E546", {"start": v(3.02, 6.79) * mm, "end": v(3.01, 6.79) * mm});
            skLineSegment(sketch, "E547", {"start": v(3.01, 6.79) * mm, "end": v(3, 6.79) * mm});
            skLineSegment(sketch, "E548", {"start": v(3, 6.79) * mm, "end": v(3, 6.79) * mm});
            skLineSegment(sketch, "E549", {"start": v(3, 6.79) * mm, "end": v(2.99, 6.79) * mm});
            skLineSegment(sketch, "E550", {"start": v(2.99, 6.79) * mm, "end": v(2.98, 6.79) * mm});
            skLineSegment(sketch, "E551", {"start": v(2.98, 6.79) * mm, "end": v(2.98, 6.79) * mm});
            skLineSegment(sketch, "E552", {"start": v(2.98, 6.79) * mm, "end": v(2.97, 6.79) * mm});
            skLineSegment(sketch, "E553", {"start": v(2.97, 6.79) * mm, "end": v(2.97, 6.79) * mm});
            skLineSegment(sketch, "E554", {"start": v(2.97, 6.79) * mm, "end": v(2.96, 6.79) * mm});
            skLineSegment(sketch, "E555", {"start": v(2.96, 6.79) * mm, "end": v(2.96, 6.79) * mm});
            skLineSegment(sketch, "E556", {"start": v(2.96, 6.79) * mm, "end": v(2.95, 6.79) * mm});
            skLineSegment(sketch, "E557", {"start": v(2.95, 6.79) * mm, "end": v(2.95, 6.79) * mm});
            skLineSegment(sketch, "E558", {"start": v(2.95, 6.79) * mm, "end": v(2.94, 6.8) * mm});
            skLineSegment(sketch, "E559", {"start": v(2.94, 6.8) * mm, "end": v(2.94, 6.8) * mm});
            skLineSegment(sketch, "E560", {"start": v(2.94, 6.8) * mm, "end": v(2.93, 6.8) * mm});
            skLineSegment(sketch, "E561", {"start": v(2.93, 6.8) * mm, "end": v(2.93, 6.8) * mm});
            skLineSegment(sketch, "E562", {"start": v(2.93, 6.8) * mm, "end": v(2.92, 6.8) * mm});
            skLineSegment(sketch, "E563", {"start": v(2.92, 6.8) * mm, "end": v(2.92, 6.8) * mm});
            skLineSegment(sketch, "E564", {"start": v(2.92, 6.8) * mm, "end": v(2.91, 6.8) * mm});
            skLineSegment(sketch, "E565", {"start": v(-0.45, 10.34) * mm, "end": v(0.3, 10.35) * mm});
            skLineSegment(sketch, "E566", {"start": v(0, 0) * mm, "end": v(-0.4, 10.34) * mm});
            skLineSegment(sketch, "E567", {"start": v(0, 0) * mm, "end": v(0.28, 10.35) * mm});
            skLineSegment(sketch, "E568", {"start": v(0, 6.3) * mm, "end": v(2.91, 6.8) * mm});
            skLineSegment(sketch, "E569", {"start": v(0, 6.3) * mm, "end": v(2.95, 6.23) * mm});
            skCircle(sketch, "E570", {"center": v(0, 6.3) * mm, "radius": 1.35 * mm});
            skLineSegment(sketch, "E571", {"start": v(0, 0) * mm, "end": v(2.8, -0.5) * mm});
            skLineSegment(sketch, "E572", {"start": v(0, 0) * mm, "end": v(2.85, 0.07) * mm});
            skCircle(sketch, "E573", {"center": v(0, 0) * mm, "radius": 1.35 * mm});
            skSolve(sketch);
        }
        {
            var Q0;
            {var subQ3=sQuery(id+"F0.wireOp",EDGE,"E571");var subQ5=sQuery(id+"F0.wireOp",EDGE,"E1");var subQ7=makeQuery(id+"F0.imprint","INTERSECT",VERTEX,{"derivedFrom":[subQ5,subQ3]});Q0=makeQuery(id+"F0.imprint","IMPRINT",FACE,{"disambiguationData":[TD([[makeQuery(id+"F0.imprint","IMPRINT",EDGE,{"disambiguationData":[TD([[subQ7,1.0]])],"derivedFrom":subQ5}),1.0]])]});}
            var Q1;
            {var subQ4=sQuery(id+"F0.wireOp",EDGE,"E214");Q1=makeQuery(id+"F0.imprint","IMPRINT",FACE,{"disambiguationData":[TD([[makeQuery(id+"F0.imprint","IMPRINT",EDGE,{"derivedFrom":subQ4}),1.0]])]});}
            var Q2;
            {var subQ1=sQuery(id+"F0.wireOp",EDGE,"E1");var subQ3=sQuery(id+"F0.wireOp",EDGE,"E571");var subQ5=makeQuery(id+"F0.imprint","INTERSECT",VERTEX,{"derivedFrom":[subQ1,subQ3]});Q2=makeQuery(id+"F0.imprint","IMPRINT",FACE,{"disambiguationData":[TD([[makeQuery(id+"F0.imprint","IMPRINT",EDGE,{"disambiguationData":[TD([[subQ5,1.0]])],"derivedFrom":subQ1}),-1.0]])]});}
            extrude(context, id + "F1", {"entities" : qUnion([Q0, Q1, Q2]), "depth" : 5 * mm});
        }
        {
            var Q0;
            Q0=makeQuery(id+"F1.opExtrude","SWEPT_BODY",BODY,{"disambiguationData":[OSD([sQuery(id+"F0.wireOp",EDGE,"E214"),sQuery(id+"F0.wireOp",EDGE,"E215"),sQuery(id+"F0.wireOp",EDGE,"E216"),sQuery(id+"F0.wireOp",EDGE,"E217"),sQuery(id+"F0.wireOp",EDGE,"E218"),sQuery(id+"F0.wireOp",EDGE,"E219"),sQuery(id+"F0.wireOp",EDGE,"E220"),sQuery(id+"F0.wireOp",EDGE,"E221"),sQuery(id+"F0.wireOp",EDGE,"E222"),sQuery(id+"F0.wireOp",EDGE,"E223"),sQuery(id+"F0.wireOp",EDGE,"E223"),sQuery(id+"F0.wireOp",EDGE,"E224"),sQuery(id+"F0.wireOp",EDGE,"E225"),sQuery(id+"F0.wireOp",EDGE,"E226"),sQuery(id+"F0.wireOp",EDGE,"E227"),sQuery(id+"F0.wireOp",EDGE,"E228"),sQuery(id+"F0.wireOp",EDGE,"E228"),sQuery(id+"F0.wireOp",EDGE,"E228"),sQuery(id+"F0.wireOp",EDGE,"E229"),sQuery(id+"F0.wireOp",EDGE,"E230"),sQuery(id+"F0.wireOp",EDGE,"E231"),sQuery(id+"F0.wireOp",EDGE,"E231"),sQuery(id+"F0.wireOp",EDGE,"E232"),sQuery(id+"F0.wireOp",EDGE,"E233"),sQuery(id+"F0.wireOp",EDGE,"E234"),sQuery(id+"F0.wireOp",EDGE,"E235"),sQuery(id+"F0.wireOp",EDGE,"E236"),sQuery(id+"F0.wireOp",EDGE,"E237"),sQuery(id+"F0.wireOp",EDGE,"E238"),sQuery(id+"F0.wireOp",EDGE,"E239"),sQuery(id+"F0.wireOp",EDGE,"E240"),sQuery(id+"F0.wireOp",EDGE,"E241"),sQuery(id+"F0.wireOp",EDGE,"E242"),sQuery(id+"F0.wireOp",EDGE,"E243"),sQuery(id+"F0.wireOp",EDGE,"E243"),sQuery(id+"F0.wireOp",EDGE,"E244"),sQuery(id+"F0.wireOp",EDGE,"E245"),sQuery(id+"F0.wireOp",EDGE,"E246"),sQuery(id+"F0.wireOp",EDGE,"E246"),sQuery(id+"F0.wireOp",EDGE,"E246"),sQuery(id+"F0.wireOp",EDGE,"E247"),sQuery(id+"F0.wireOp",EDGE,"E248"),sQuery(id+"F0.wireOp",EDGE,"E249"),sQuery(id+"F0.wireOp",EDGE,"E250"),sQuery(id+"F0.wireOp",EDGE,"E251"),sQuery(id+"F0.wireOp",EDGE,"E252"),sQuery(id+"F0.wireOp",EDGE,"E253"),sQuery(id+"F0.wireOp",EDGE,"E253"),sQuery(id+"F0.wireOp",EDGE,"E254"),sQuery(id+"F0.wireOp",EDGE,"E255"),sQuery(id+"F0.wireOp",EDGE,"E256"),sQuery(id+"F0.wireOp",EDGE,"E257"),sQuery(id+"F0.wireOp",EDGE,"E258"),sQuery(id+"F0.wireOp",EDGE,"E259"),sQuery(id+"F0.wireOp",EDGE,"E260"),sQuery(id+"F0.wireOp",EDGE,"E261"),sQuery(id+"F0.wireOp",EDGE,"E262"),sQuery(id+"F0.wireOp",EDGE,"E263"),sQuery(id+"F0.wireOp",EDGE,"E264"),sQuery(id+"F0.wireOp",EDGE,"E265"),sQuery(id+"F0.wireOp",EDGE,"E266"),sQuery(id+"F0.wireOp",EDGE,"E266"),sQuery(id+"F0.wireOp",EDGE,"E267"),sQuery(id+"F0.wireOp",EDGE,"E268"),sQuery(id+"F0.wireOp",EDGE,"E269"),sQuery(id+"F0.wireOp",EDGE,"E270"),sQuery(id+"F0.wireOp",EDGE,"E271"),sQuery(id+"F0.wireOp",EDGE,"E272"),sQuery(id+"F0.wireOp",EDGE,"E273"),sQuery(id+"F0.wireOp",EDGE,"E274"),sQuery(id+"F0.wireOp",EDGE,"E275"),sQuery(id+"F0.wireOp",EDGE,"E276"),sQuery(id+"F0.wireOp",EDGE,"E277"),sQuery(id+"F0.wireOp",EDGE,"E278"),sQuery(id+"F0.wireOp",EDGE,"E279"),sQuery(id+"F0.wireOp",EDGE,"E279"),sQuery(id+"F0.wireOp",EDGE,"E280"),sQuery(id+"F0.wireOp",EDGE,"E281"),sQuery(id+"F0.wireOp",EDGE,"E282"),sQuery(id+"F0.wireOp",EDGE,"E283"),sQuery(id+"F0.wireOp",EDGE,"E284"),sQuery(id+"F0.wireOp",EDGE,"E284"),sQuery(id+"F0.wireOp",EDGE,"E284"),sQuery(id+"F0.wireOp",EDGE,"E285"),sQuery(id+"F0.wireOp",EDGE,"E286"),sQuery(id+"F0.wireOp",EDGE,"E287"),sQuery(id+"F0.wireOp",EDGE,"E288"),sQuery(id+"F0.wireOp",EDGE,"E289"),sQuery(id+"F0.wireOp",EDGE,"E290"),sQuery(id+"F0.wireOp",EDGE,"E291"),sQuery(id+"F0.wireOp",EDGE,"E291"),sQuery(id+"F0.wireOp",EDGE,"E292"),sQuery(id+"F0.wireOp",EDGE,"E293"),sQuery(id+"F0.wireOp",EDGE,"E294"),sQuery(id+"F0.wireOp",EDGE,"E295"),sQuery(id+"F0.wireOp",EDGE,"E296"),sQuery(id+"F0.wireOp",EDGE,"E297"),sQuery(id+"F0.wireOp",EDGE,"E298"),sQuery(id+"F0.wireOp",EDGE,"E299"),sQuery(id+"F0.wireOp",EDGE,"E300"),sQuery(id+"F0.wireOp",EDGE,"E301"),sQuery(id+"F0.wireOp",EDGE,"E302"),sQuery(id+"F0.wireOp",EDGE,"E303"),sQuery(id+"F0.wireOp",EDGE,"E304"),sQuery(id+"F0.wireOp",EDGE,"E305"),sQuery(id+"F0.wireOp",EDGE,"E306"),sQuery(id+"F0.wireOp",EDGE,"E307"),sQuery(id+"F0.wireOp",EDGE,"E308"),sQuery(id+"F0.wireOp",EDGE,"E309"),sQuery(id+"F0.wireOp",EDGE,"E310"),sQuery(id+"F0.wireOp",EDGE,"E311"),sQuery(id+"F0.wireOp",EDGE,"E312"),sQuery(id+"F0.wireOp",EDGE,"E313"),sQuery(id+"F0.wireOp",EDGE,"E314"),sQuery(id+"F0.wireOp",EDGE,"E315"),sQuery(id+"F0.wireOp",EDGE,"E316"),sQuery(id+"F0.wireOp",EDGE,"E317"),sQuery(id+"F0.wireOp",EDGE,"E318"),sQuery(id+"F0.wireOp",EDGE,"E319"),sQuery(id+"F0.wireOp",EDGE,"E320"),sQuery(id+"F0.wireOp",EDGE,"E321"),sQuery(id+"F0.wireOp",EDGE,"E322"),sQuery(id+"F0.wireOp",EDGE,"E323"),sQuery(id+"F0.wireOp",EDGE,"E324"),sQuery(id+"F0.wireOp",EDGE,"E324"),sQuery(id+"F0.wireOp",EDGE,"E324"),sQuery(id+"F0.wireOp",EDGE,"E325"),sQuery(id+"F0.wireOp",EDGE,"E326"),sQuery(id+"F0.wireOp",EDGE,"E327"),sQuery(id+"F0.wireOp",EDGE,"E328"),sQuery(id+"F0.wireOp",EDGE,"E329"),sQuery(id+"F0.wireOp",EDGE,"E330"),sQuery(id+"F0.wireOp",EDGE,"E331"),sQuery(id+"F0.wireOp",EDGE,"E332"),sQuery(id+"F0.wireOp",EDGE,"E333"),sQuery(id+"F0.wireOp",EDGE,"E334"),sQuery(id+"F0.wireOp",EDGE,"E335"),sQuery(id+"F0.wireOp",EDGE,"E336"),sQuery(id+"F0.wireOp",EDGE,"E337"),sQuery(id+"F0.wireOp",EDGE,"E338"),sQuery(id+"F0.wireOp",EDGE,"E339"),sQuery(id+"F0.wireOp",EDGE,"E340"),sQuery(id+"F0.wireOp",EDGE,"E340"),sQuery(id+"F0.wireOp",EDGE,"E341"),sQuery(id+"F0.wireOp",EDGE,"E342"),sQuery(id+"F0.wireOp",EDGE,"E343"),sQuery(id+"F0.wireOp",EDGE,"E343"),sQuery(id+"F0.wireOp",EDGE,"E343"),sQuery(id+"F0.wireOp",EDGE,"E344"),sQuery(id+"F0.wireOp",EDGE,"E345"),sQuery(id+"F0.wireOp",EDGE,"E346"),sQuery(id+"F0.wireOp",EDGE,"E347"),sQuery(id+"F0.wireOp",EDGE,"E348"),sQuery(id+"F0.wireOp",EDGE,"E349"),sQuery(id+"F0.wireOp",EDGE,"E350"),sQuery(id+"F0.wireOp",EDGE,"E351"),sQuery(id+"F0.wireOp",EDGE,"E352"),sQuery(id+"F0.wireOp",EDGE,"E353"),sQuery(id+"F0.wireOp",EDGE,"E354"),sQuery(id+"F0.wireOp",EDGE,"E355"),sQuery(id+"F0.wireOp",EDGE,"E356"),sQuery(id+"F0.wireOp",EDGE,"E357"),sQuery(id+"F0.wireOp",EDGE,"E357"),sQuery(id+"F0.wireOp",EDGE,"E358"),sQuery(id+"F0.wireOp",EDGE,"E359"),sQuery(id+"F0.wireOp",EDGE,"E360"),sQuery(id+"F0.wireOp",EDGE,"E361"),sQuery(id+"F0.wireOp",EDGE,"E362"),sQuery(id+"F0.wireOp",EDGE,"E362"),sQuery(id+"F0.wireOp",EDGE,"E362"),sQuery(id+"F0.wireOp",EDGE,"E363"),sQuery(id+"F0.wireOp",EDGE,"E364"),sQuery(id+"F0.wireOp",EDGE,"E365"),sQuery(id+"F0.wireOp",EDGE,"E366"),sQuery(id+"F0.wireOp",EDGE,"E367"),sQuery(id+"F0.wireOp",EDGE,"E368"),sQuery(id+"F0.wireOp",EDGE,"E369"),sQuery(id+"F0.wireOp",EDGE,"E370"),sQuery(id+"F0.wireOp",EDGE,"E371"),sQuery(id+"F0.wireOp",EDGE,"E372"),sQuery(id+"F0.wireOp",EDGE,"E373"),sQuery(id+"F0.wireOp",EDGE,"E374"),sQuery(id+"F0.wireOp",EDGE,"E374"),sQuery(id+"F0.wireOp",EDGE,"E375"),sQuery(id+"F0.wireOp",EDGE,"E376"),sQuery(id+"F0.wireOp",EDGE,"E377"),sQuery(id+"F0.wireOp",EDGE,"E378"),sQuery(id+"F0.wireOp",EDGE,"E379"),sQuery(id+"F0.wireOp",EDGE,"E380"),sQuery(id+"F0.wireOp",EDGE,"E381"),sQuery(id+"F0.wireOp",EDGE,"E381"),sQuery(id+"F0.wireOp",EDGE,"E381"),sQuery(id+"F0.wireOp",EDGE,"E381"),sQuery(id+"F0.wireOp",EDGE,"E382"),sQuery(id+"F0.wireOp",EDGE,"E383"),sQuery(id+"F0.wireOp",EDGE,"E384"),sQuery(id+"F0.wireOp",EDGE,"E385"),sQuery(id+"F0.wireOp",EDGE,"E386"),sQuery(id+"F0.wireOp",EDGE,"E387"),sQuery(id+"F0.wireOp",EDGE,"E388"),sQuery(id+"F0.wireOp",EDGE,"E389"),sQuery(id+"F0.wireOp",EDGE,"E571"),sQuery(id+"F0.wireOp",EDGE,"E572")])]});
            var Q1;
            Q1=makeQuery(id+"F1.opExtrude","SWEPT_EDGE",EDGE,{"disambiguationData":[OSD([sQuery(id+"F0.wireOp",EDGE,"E566"),sQuery(id+"F0.wireOp",EDGE,"E567"),sQuery(id+"F0.wireOp",EDGE,"E571"),sQuery(id+"F0.wireOp",EDGE,"E572")])]});
            circularPattern(context, id + "F2", {"operationType" : NewBodyOperationType.ADD, "entities" : qUnion([Q0]), "axis" : qUnion([Q1]), "angle" : 11.6 * degree, "instanceCount" : round(31)});
        }
        {
            var Q0;
            {var subQ3=sQuery(id+"F0.wireOp",EDGE,"E566");var subQ5=sQuery(id+"F0.wireOp",EDGE,"E1");var subQ7=makeQuery(id+"F0.imprint","INTERSECT",VERTEX,{"derivedFrom":[subQ5,subQ3]});Q0=makeQuery(id+"F0.imprint","IMPRINT",FACE,{"disambiguationData":[TD([[makeQuery(id+"F0.imprint","IMPRINT",EDGE,{"disambiguationData":[TD([[subQ7,1.0]])],"derivedFrom":subQ5}),1.0]])]});}
            var Q1;
            {var subQ3=sQuery(id+"F0.wireOp",EDGE,"E571");var subQ5=sQuery(id+"F0.wireOp",EDGE,"E1");var subQ7=makeQuery(id+"F0.imprint","INTERSECT",VERTEX,{"derivedFrom":[subQ5,subQ3]});Q1=makeQuery(id+"F0.imprint","IMPRINT",FACE,{"disambiguationData":[TD([[makeQuery(id+"F0.imprint","IMPRINT",EDGE,{"disambiguationData":[TD([[subQ7,1.0]])],"derivedFrom":subQ5}),1.0]])]});}
            var Q2;
            {var subQ3=sQuery(id+"F0.wireOp",EDGE,"E567");var subQ5=sQuery(id+"F0.wireOp",EDGE,"E1");var subQ7=makeQuery(id+"F0.imprint","INTERSECT",VERTEX,{"derivedFrom":[subQ5,subQ3]});Q2=makeQuery(id+"F0.imprint","IMPRINT",FACE,{"disambiguationData":[TD([[makeQuery(id+"F0.imprint","IMPRINT",EDGE,{"disambiguationData":[TD([[subQ7,-1.0]])],"derivedFrom":subQ5}),1.0]])]});}
            var Q3;
            {var subQ3=sQuery(id+"F0.wireOp",EDGE,"E566");var subQ5=sQuery(id+"F0.wireOp",EDGE,"E1");var subQ7=makeQuery(id+"F0.imprint","INTERSECT",VERTEX,{"derivedFrom":[subQ5,subQ3]});Q3=makeQuery(id+"F0.imprint","IMPRINT",FACE,{"disambiguationData":[TD([[makeQuery(id+"F0.imprint","IMPRINT",EDGE,{"disambiguationData":[TD([[subQ7,-1.0]])],"derivedFrom":subQ5}),1.0]])]});}
            var Q4;
            {var subQ1=sQuery(id+"F0.wireOp",EDGE,"E1");var subQ3=sQuery(id+"F0.wireOp",EDGE,"E566");var subQ5=makeQuery(id+"F0.imprint","INTERSECT",VERTEX,{"derivedFrom":[subQ1,subQ3]});Q4=makeQuery(id+"F0.imprint","IMPRINT",FACE,{"disambiguationData":[TD([[makeQuery(id+"F0.imprint","IMPRINT",EDGE,{"disambiguationData":[TD([[subQ5,1.0]])],"derivedFrom":subQ1}),-1.0]])]});}
            var Q5;
            {var subQ1=sQuery(id+"F0.wireOp",EDGE,"E1");var subQ3=sQuery(id+"F0.wireOp",EDGE,"E571");var subQ5=makeQuery(id+"F0.imprint","INTERSECT",VERTEX,{"derivedFrom":[subQ1,subQ3]});Q5=makeQuery(id+"F0.imprint","IMPRINT",FACE,{"disambiguationData":[TD([[makeQuery(id+"F0.imprint","IMPRINT",EDGE,{"disambiguationData":[TD([[subQ5,1.0]])],"derivedFrom":subQ1}),-1.0]])]});}
            var Q6;
            {var subQ1=sQuery(id+"F0.wireOp",EDGE,"E1");var subQ3=sQuery(id+"F0.wireOp",EDGE,"E567");var subQ5=makeQuery(id+"F0.imprint","INTERSECT",VERTEX,{"derivedFrom":[subQ1,subQ3]});Q6=makeQuery(id+"F0.imprint","IMPRINT",FACE,{"disambiguationData":[TD([[makeQuery(id+"F0.imprint","IMPRINT",EDGE,{"disambiguationData":[TD([[subQ5,-1.0]])],"derivedFrom":subQ1}),-1.0]])]});}
            var Q7;
            {var subQ1=sQuery(id+"F0.wireOp",EDGE,"E1");var subQ3=sQuery(id+"F0.wireOp",EDGE,"E566");var subQ5=makeQuery(id+"F0.imprint","INTERSECT",VERTEX,{"derivedFrom":[subQ1,subQ3]});Q7=makeQuery(id+"F0.imprint","IMPRINT",FACE,{"disambiguationData":[TD([[makeQuery(id+"F0.imprint","IMPRINT",EDGE,{"disambiguationData":[TD([[subQ5,-1.0]])],"derivedFrom":subQ1}),-1.0]])]});}
            extrude(context, id + "F3", {"entities" : qUnion([Q0, Q1, Q2, Q3, Q4, Q5, Q6, Q7]), "operationType" : NewBodyOperationType.REMOVE, "endBound" : BoundingType.UP_TO_NEXT, "depth" : 25 * mm});
        }
        {
            var Q0;
            {var subQ0=makeQuery(id+"F1.opExtrude","CAP_FACE",FACE,{"disambiguationData":[OSD([sQuery(id+"F0.wireOp",EDGE,"E214"),sQuery(id+"F0.wireOp",EDGE,"E215"),sQuery(id+"F0.wireOp",EDGE,"E216"),sQuery(id+"F0.wireOp",EDGE,"E217"),sQuery(id+"F0.wireOp",EDGE,"E218"),sQuery(id+"F0.wireOp",EDGE,"E219"),sQuery(id+"F0.wireOp",EDGE,"E220"),sQuery(id+"F0.wireOp",EDGE,"E221"),sQuery(id+"F0.wireOp",EDGE,"E222"),sQuery(id+"F0.wireOp",EDGE,"E223"),sQuery(id+"F0.wireOp",EDGE,"E223"),sQuery(id+"F0.wireOp",EDGE,"E224"),sQuery(id+"F0.wireOp",EDGE,"E225"),sQuery(id+"F0.wireOp",EDGE,"E226"),sQuery(id+"F0.wireOp",EDGE,"E227"),sQuery(id+"F0.wireOp",EDGE,"E228"),sQuery(id+"F0.wireOp",EDGE,"E228"),sQuery(id+"F0.wireOp",EDGE,"E228"),sQuery(id+"F0.wireOp",EDGE,"E229"),sQuery(id+"F0.wireOp",EDGE,"E230"),sQuery(id+"F0.wireOp",EDGE,"E231"),sQuery(id+"F0.wireOp",EDGE,"E231"),sQuery(id+"F0.wireOp",EDGE,"E232"),sQuery(id+"F0.wireOp",EDGE,"E233"),sQuery(id+"F0.wireOp",EDGE,"E234"),sQuery(id+"F0.wireOp",EDGE,"E235"),sQuery(id+"F0.wireOp",EDGE,"E236"),sQuery(id+"F0.wireOp",EDGE,"E237"),sQuery(id+"F0.wireOp",EDGE,"E238"),sQuery(id+"F0.wireOp",EDGE,"E239"),sQuery(id+"F0.wireOp",EDGE,"E240"),sQuery(id+"F0.wireOp",EDGE,"E241"),sQuery(id+"F0.wireOp",EDGE,"E242"),sQuery(id+"F0.wireOp",EDGE,"E243"),sQuery(id+"F0.wireOp",EDGE,"E243"),sQuery(id+"F0.wireOp",EDGE,"E244"),sQuery(id+"F0.wireOp",EDGE,"E245"),sQuery(id+"F0.wireOp",EDGE,"E246"),sQuery(id+"F0.wireOp",EDGE,"E246"),sQuery(id+"F0.wireOp",EDGE,"E246"),sQuery(id+"F0.wireOp",EDGE,"E247"),sQuery(id+"F0.wireOp",EDGE,"E248"),sQuery(id+"F0.wireOp",EDGE,"E249"),sQuery(id+"F0.wireOp",EDGE,"E250"),sQuery(id+"F0.wireOp",EDGE,"E251"),sQuery(id+"F0.wireOp",EDGE,"E252"),sQuery(id+"F0.wireOp",EDGE,"E253"),sQuery(id+"F0.wireOp",EDGE,"E253"),sQuery(id+"F0.wireOp",EDGE,"E254"),sQuery(id+"F0.wireOp",EDGE,"E255"),sQuery(id+"F0.wireOp",EDGE,"E256"),sQuery(id+"F0.wireOp",EDGE,"E257"),sQuery(id+"F0.wireOp",EDGE,"E258"),sQuery(id+"F0.wireOp",EDGE,"E259"),sQuery(id+"F0.wireOp",EDGE,"E260"),sQuery(id+"F0.wireOp",EDGE,"E261"),sQuery(id+"F0.wireOp",EDGE,"E262"),sQuery(id+"F0.wireOp",EDGE,"E263"),sQuery(id+"F0.wireOp",EDGE,"E264"),sQuery(id+"F0.wireOp",EDGE,"E265"),sQuery(id+"F0.wireOp",EDGE,"E266"),sQuery(id+"F0.wireOp",EDGE,"E266"),sQuery(id+"F0.wireOp",EDGE,"E267"),sQuery(id+"F0.wireOp",EDGE,"E268"),sQuery(id+"F0.wireOp",EDGE,"E269"),sQuery(id+"F0.wireOp",EDGE,"E270"),sQuery(id+"F0.wireOp",EDGE,"E271"),sQuery(id+"F0.wireOp",EDGE,"E272"),sQuery(id+"F0.wireOp",EDGE,"E273"),sQuery(id+"F0.wireOp",EDGE,"E274"),sQuery(id+"F0.wireOp",EDGE,"E275"),sQuery(id+"F0.wireOp",EDGE,"E276"),sQuery(id+"F0.wireOp",EDGE,"E277"),sQuery(id+"F0.wireOp",EDGE,"E278"),sQuery(id+"F0.wireOp",EDGE,"E279"),sQuery(id+"F0.wireOp",EDGE,"E279"),sQuery(id+"F0.wireOp",EDGE,"E280"),sQuery(id+"F0.wireOp",EDGE,"E281"),sQuery(id+"F0.wireOp",EDGE,"E282"),sQuery(id+"F0.wireOp",EDGE,"E283"),sQuery(id+"F0.wireOp",EDGE,"E284"),sQuery(id+"F0.wireOp",EDGE,"E284"),sQuery(id+"F0.wireOp",EDGE,"E284"),sQuery(id+"F0.wireOp",EDGE,"E285"),sQuery(id+"F0.wireOp",EDGE,"E286"),sQuery(id+"F0.wireOp",EDGE,"E287"),sQuery(id+"F0.wireOp",EDGE,"E288"),sQuery(id+"F0.wireOp",EDGE,"E289"),sQuery(id+"F0.wireOp",EDGE,"E290"),sQuery(id+"F0.wireOp",EDGE,"E291"),sQuery(id+"F0.wireOp",EDGE,"E291"),sQuery(id+"F0.wireOp",EDGE,"E292"),sQuery(id+"F0.wireOp",EDGE,"E293"),sQuery(id+"F0.wireOp",EDGE,"E294"),sQuery(id+"F0.wireOp",EDGE,"E295"),sQuery(id+"F0.wireOp",EDGE,"E296"),sQuery(id+"F0.wireOp",EDGE,"E297"),sQuery(id+"F0.wireOp",EDGE,"E298"),sQuery(id+"F0.wireOp",EDGE,"E299"),sQuery(id+"F0.wireOp",EDGE,"E300"),sQuery(id+"F0.wireOp",EDGE,"E301"),sQuery(id+"F0.wireOp",EDGE,"E302"),sQuery(id+"F0.wireOp",EDGE,"E303"),sQuery(id+"F0.wireOp",EDGE,"E304"),sQuery(id+"F0.wireOp",EDGE,"E305"),sQuery(id+"F0.wireOp",EDGE,"E306"),sQuery(id+"F0.wireOp",EDGE,"E307"),sQuery(id+"F0.wireOp",EDGE,"E308"),sQuery(id+"F0.wireOp",EDGE,"E309"),sQuery(id+"F0.wireOp",EDGE,"E310"),sQuery(id+"F0.wireOp",EDGE,"E311"),sQuery(id+"F0.wireOp",EDGE,"E312"),sQuery(id+"F0.wireOp",EDGE,"E313"),sQuery(id+"F0.wireOp",EDGE,"E314"),sQuery(id+"F0.wireOp",EDGE,"E315"),sQuery(id+"F0.wireOp",EDGE,"E316"),sQuery(id+"F0.wireOp",EDGE,"E317"),sQuery(id+"F0.wireOp",EDGE,"E318"),sQuery(id+"F0.wireOp",EDGE,"E319"),sQuery(id+"F0.wireOp",EDGE,"E320"),sQuery(id+"F0.wireOp",EDGE,"E321"),sQuery(id+"F0.wireOp",EDGE,"E322"),sQuery(id+"F0.wireOp",EDGE,"E323"),sQuery(id+"F0.wireOp",EDGE,"E324"),sQuery(id+"F0.wireOp",EDGE,"E324"),sQuery(id+"F0.wireOp",EDGE,"E324"),sQuery(id+"F0.wireOp",EDGE,"E325"),sQuery(id+"F0.wireOp",EDGE,"E326"),sQuery(id+"F0.wireOp",EDGE,"E327"),sQuery(id+"F0.wireOp",EDGE,"E328"),sQuery(id+"F0.wireOp",EDGE,"E329"),sQuery(id+"F0.wireOp",EDGE,"E330"),sQuery(id+"F0.wireOp",EDGE,"E331"),sQuery(id+"F0.wireOp",EDGE,"E332"),sQuery(id+"F0.wireOp",EDGE,"E333"),sQuery(id+"F0.wireOp",EDGE,"E334"),sQuery(id+"F0.wireOp",EDGE,"E335"),sQuery(id+"F0.wireOp",EDGE,"E336"),sQuery(id+"F0.wireOp",EDGE,"E337"),sQuery(id+"F0.wireOp",EDGE,"E338"),sQuery(id+"F0.wireOp",EDGE,"E339"),sQuery(id+"F0.wireOp",EDGE,"E340"),sQuery(id+"F0.wireOp",EDGE,"E340"),sQuery(id+"F0.wireOp",EDGE,"E341"),sQuery(id+"F0.wireOp",EDGE,"E342"),sQuery(id+"F0.wireOp",EDGE,"E343"),sQuery(id+"F0.wireOp",EDGE,"E343"),sQuery(id+"F0.wireOp",EDGE,"E343"),sQuery(id+"F0.wireOp",EDGE,"E344"),sQuery(id+"F0.wireOp",EDGE,"E345"),sQuery(id+"F0.wireOp",EDGE,"E346"),sQuery(id+"F0.wireOp",EDGE,"E347"),sQuery(id+"F0.wireOp",EDGE,"E348"),sQuery(id+"F0.wireOp",EDGE,"E349"),sQuery(id+"F0.wireOp",EDGE,"E350"),sQuery(id+"F0.wireOp",EDGE,"E351"),sQuery(id+"F0.wireOp",EDGE,"E352"),sQuery(id+"F0.wireOp",EDGE,"E353"),sQuery(id+"F0.wireOp",EDGE,"E354"),sQuery(id+"F0.wireOp",EDGE,"E355"),sQuery(id+"F0.wireOp",EDGE,"E356"),sQuery(id+"F0.wireOp",EDGE,"E357"),sQuery(id+"F0.wireOp",EDGE,"E357"),sQuery(id+"F0.wireOp",EDGE,"E358"),sQuery(id+"F0.wireOp",EDGE,"E359"),sQuery(id+"F0.wireOp",EDGE,"E360"),sQuery(id+"F0.wireOp",EDGE,"E361"),sQuery(id+"F0.wireOp",EDGE,"E362"),sQuery(id+"F0.wireOp",EDGE,"E362"),sQuery(id+"F0.wireOp",EDGE,"E362"),sQuery(id+"F0.wireOp",EDGE,"E363"),sQuery(id+"F0.wireOp",EDGE,"E364"),sQuery(id+"F0.wireOp",EDGE,"E365"),sQuery(id+"F0.wireOp",EDGE,"E366"),sQuery(id+"F0.wireOp",EDGE,"E367"),sQuery(id+"F0.wireOp",EDGE,"E368"),sQuery(id+"F0.wireOp",EDGE,"E369"),sQuery(id+"F0.wireOp",EDGE,"E370"),sQuery(id+"F0.wireOp",EDGE,"E371"),sQuery(id+"F0.wireOp",EDGE,"E372"),sQuery(id+"F0.wireOp",EDGE,"E373"),sQuery(id+"F0.wireOp",EDGE,"E374"),sQuery(id+"F0.wireOp",EDGE,"E374"),sQuery(id+"F0.wireOp",EDGE,"E375"),sQuery(id+"F0.wireOp",EDGE,"E376"),sQuery(id+"F0.wireOp",EDGE,"E377"),sQuery(id+"F0.wireOp",EDGE,"E378"),sQuery(id+"F0.wireOp",EDGE,"E379"),sQuery(id+"F0.wireOp",EDGE,"E380"),sQuery(id+"F0.wireOp",EDGE,"E381"),sQuery(id+"F0.wireOp",EDGE,"E381"),sQuery(id+"F0.wireOp",EDGE,"E381"),sQuery(id+"F0.wireOp",EDGE,"E381"),sQuery(id+"F0.wireOp",EDGE,"E382"),sQuery(id+"F0.wireOp",EDGE,"E383"),sQuery(id+"F0.wireOp",EDGE,"E384"),sQuery(id+"F0.wireOp",EDGE,"E385"),sQuery(id+"F0.wireOp",EDGE,"E386"),sQuery(id+"F0.wireOp",EDGE,"E387"),sQuery(id+"F0.wireOp",EDGE,"E388"),sQuery(id+"F0.wireOp",EDGE,"E389"),sQuery(id+"F0.wireOp",EDGE,"E571"),sQuery(id+"F0.wireOp",EDGE,"E572")])],"isStart":false});Q0=makeQuery(id+"F2.boolean.opBoolean","MERGE",FACE,{"derivedFrom":[subQ0,makeQuery(id+"F2.opPattern","COPY",FACE,{"derivedFrom":subQ0,"instanceName":"1"}),makeQuery(id+"F2.opPattern","COPY",FACE,{"derivedFrom":subQ0,"instanceName":"2"}),makeQuery(id+"F2.opPattern","COPY",FACE,{"derivedFrom":subQ0,"instanceName":"3"}),makeQuery(id+"F2.opPattern","COPY",FACE,{"derivedFrom":subQ0,"instanceName":"4"}),makeQuery(id+"F2.opPattern","COPY",FACE,{"derivedFrom":subQ0,"instanceName":"5"}),makeQuery(id+"F2.opPattern","COPY",FACE,{"derivedFrom":subQ0,"instanceName":"6"}),makeQuery(id+"F2.opPattern","COPY",FACE,{"derivedFrom":subQ0,"instanceName":"7"}),makeQuery(id+"F2.opPattern","COPY",FACE,{"derivedFrom":subQ0,"instanceName":"8"}),makeQuery(id+"F2.opPattern","COPY",FACE,{"derivedFrom":subQ0,"instanceName":"9"}),makeQuery(id+"F2.opPattern","COPY",FACE,{"derivedFrom":subQ0,"instanceName":"10"}),makeQuery(id+"F2.opPattern","COPY",FACE,{"derivedFrom":subQ0,"instanceName":"11"}),makeQuery(id+"F2.opPattern","COPY",FACE,{"derivedFrom":subQ0,"instanceName":"12"}),makeQuery(id+"F2.opPattern","COPY",FACE,{"derivedFrom":subQ0,"instanceName":"13"}),makeQuery(id+"F2.opPattern","COPY",FACE,{"derivedFrom":subQ0,"instanceName":"14"}),makeQuery(id+"F2.opPattern","COPY",FACE,{"derivedFrom":subQ0,"instanceName":"15"}),makeQuery(id+"F2.opPattern","COPY",FACE,{"derivedFrom":subQ0,"instanceName":"16"}),makeQuery(id+"F2.opPattern","COPY",FACE,{"derivedFrom":subQ0,"instanceName":"17"}),makeQuery(id+"F2.opPattern","COPY",FACE,{"derivedFrom":subQ0,"instanceName":"18"}),makeQuery(id+"F2.opPattern","COPY",FACE,{"derivedFrom":subQ0,"instanceName":"19"}),makeQuery(id+"F2.opPattern","COPY",FACE,{"derivedFrom":subQ0,"instanceName":"20"}),makeQuery(id+"F2.opPattern","COPY",FACE,{"derivedFrom":subQ0,"instanceName":"21"}),makeQuery(id+"F2.opPattern","COPY",FACE,{"derivedFrom":subQ0,"instanceName":"22"}),makeQuery(id+"F2.opPattern","COPY",FACE,{"derivedFrom":subQ0,"instanceName":"23"}),makeQuery(id+"F2.opPattern","COPY",FACE,{"derivedFrom":subQ0,"instanceName":"24"}),makeQuery(id+"F2.opPattern","COPY",FACE,{"derivedFrom":subQ0,"instanceName":"25"}),makeQuery(id+"F2.opPattern","COPY",FACE,{"derivedFrom":subQ0,"instanceName":"26"}),makeQuery(id+"F2.opPattern","COPY",FACE,{"derivedFrom":subQ0,"instanceName":"27"}),makeQuery(id+"F2.opPattern","COPY",FACE,{"derivedFrom":subQ0,"instanceName":"28"}),makeQuery(id+"F2.opPattern","COPY",FACE,{"derivedFrom":subQ0,"instanceName":"29"}),makeQuery(id+"F2.opPattern","COPY",FACE,{"derivedFrom":subQ0,"instanceName":"30"})]});}
            var sketch = newSketch(context, id + "F4", { "sketchPlane" : qUnion([Q0])});
            skText(sketch, "E574", { "text": "31", "fontName": "OpenSans-Bold.ttf"});
            const initialGuessF4  = {"E574": [-0.00265, -0.0005, 1, 0, 0.00082]};
            skSetInitialGuess(sketch, initialGuessF4);
            skSolve(sketch);
        }
        {
            var Q0;
            Q0=makeQuery(id+"F4.imprint","IMPRINT",FACE,{"disambiguationData":[TD([[makeQuery(id+"F4.imprint","IMPRINT",EDGE,{"derivedFrom":sQuery(id+"F4.wireOp",EDGE,"E574.sketch_text.stroke-0")}),-1.0]])]});
            var Q1;
            Q1=makeQuery(id+"F4.imprint","IMPRINT",FACE,{"disambiguationData":[TD([[makeQuery(id+"F4.imprint","IMPRINT",EDGE,{"derivedFrom":sQuery(id+"F4.wireOp",EDGE,"E574.sketch_text.stroke-27")}),-1.0]])]});
            extrude(context, id + "F5", {"entities" : qUnion([Q0, Q1]), "operationType" : NewBodyOperationType.REMOVE, "oppositeDirection" : true, "depth" : .5 * mm});
        }
    });
